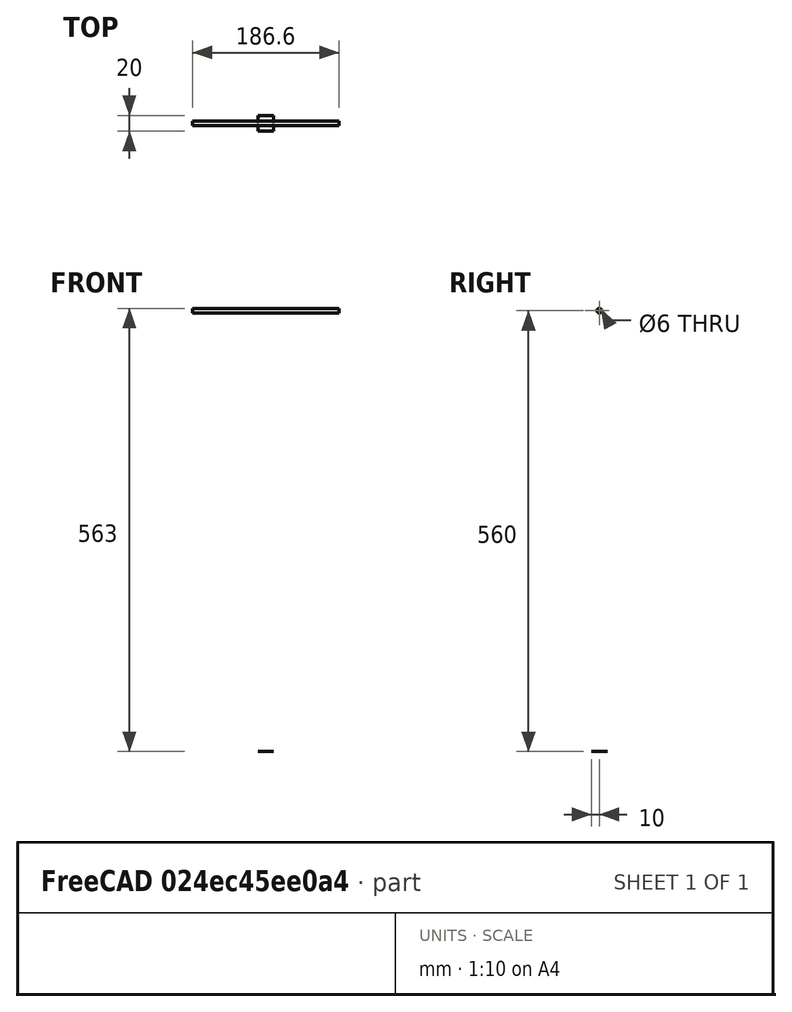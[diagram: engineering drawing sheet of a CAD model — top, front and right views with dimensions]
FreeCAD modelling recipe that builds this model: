
FCSTD DOCUMENT  (FreeCAD 0.19R18044 (Git))
Label: lift-middle-stage
License: Public Domain
LicenseURL: http://en.wikipedia.org/wiki/Public_domain
objects: App::FeaturePython×44, Part::FeaturePython×34, App::Link×6, App::LinkElement×4
note: 33 computed .brp shape members not serialized (recipe doc carries the construction recipe); baked Part::Feature solids carry a one-line shape summary decoded from their .brp
EXTERNAL_REF file=../parts/lift/middle-stage-actuator-rod.FCStd obj=Assembly
EXTERNAL_REF file=../parts/lift/middle-stage-beam.FCStd obj=Assembly001
EXTERNAL_REF file=../parts/lift/middle-stage-beam.FCStd obj=Assembly
EXTERNAL_REF file=../parts/common/linear-actuator-400.FCStd obj=Assembly004
EXTERNAL_REF file=../parts/common/rail-450.FCStd obj=Assembly002
EXTERNAL_REF file=../parts/common/rail-450.FCStd obj=Assembly

FEATURE [App::Link] Link  label="middle-stage-actuator-rod"
  LinkPlacement = pos=(0,-6.67572e-05,560) rot=(0,0,1;0rad)
  LinkedObject = -> <external ../parts/lift/middle-stage-actuator-rod.FCStd>#Assembly
  Placement = pos=(0,-6.67572e-05,560) rot=(0,0,1;0rad)
FEATURE [App::Link] Link001  label="middle-stage-beam-left"
  LinkPlacement = pos=(71.3,-24.5001,10.0001) rot=(0,0,1;0rad)
  LinkedObject = -> <external ../parts/lift/middle-stage-beam.FCStd>#Assembly001
  Placement = pos=(71.3,-24.5001,10.0001) rot=(0,0,1;0rad)
FEATURE [App::Link] Link002  label="middle-stage-beam-right"
  LinkPlacement = pos=(49.7,-24.5001,10.0001) rot=(0,0,1;0rad)
  LinkedObject = -> <external ../parts/lift/middle-stage-beam.FCStd>#Assembly
  Placement = pos=(49.7,-24.5001,10.0001) rot=(0,0,1;0rad)
FEATURE [App::Link] Link003  label="actuator_a"
  LinkPlacement = pos=(7.1213e-12,-6.67572e-05,44.0001) rot=(0,0,1;3.14159rad)
  LinkedObject = -> <external ../parts/common/linear-actuator-400.FCStd>#Assembly004
  Placement = pos=(7.1213e-12,-6.67572e-05,44.0001) rot=(0,0,1;3.14159rad)
FEATURE [App::LinkElement] Link004_i0  label="left"
  LinkPlacement = pos=(106,-6.67572e-05,565) rot=(0.57735,-0.57735,-0.57735;2.0944rad)
  LinkedObject = -> <external ../parts/common/rail-450.FCStd>#Assembly002
  Placement = pos=(106,-6.67572e-05,565) rot=(0.57735,-0.57735,-0.57735;2.0944rad)
FEATURE [App::LinkElement] Link004_i1  label="right"
  LinkPlacement = pos=(-106,-6.67572e-05,565) rot=(0.57735,0.57735,0.57735;2.0944rad)
  LinkedObject = -> <external ../parts/common/rail-450.FCStd>#Assembly002
  Placement = pos=(-106,-6.67572e-05,565) rot=(0.57735,0.57735,0.57735;2.0944rad)
FEATURE [App::Link] Link004  label="rail top"
  ElementCount = 2
  ElementList = -> [Link004_i0,Link004_i1]
  LinkedObject = -> <external ../parts/common/rail-450.FCStd>#Assembly002
FEATURE [App::LinkElement] Link005_i0  label="rail-upper-left"
  LinkPlacement = pos=(93.3,-49.0001,610) rot=(0.57735,0.57735,0.57735;2.0944rad)
  LinkedObject = -> <external ../parts/common/rail-450.FCStd>#Assembly
  Placement = pos=(93.3,-49.0001,610) rot=(0.57735,0.57735,0.57735;2.0944rad)
FEATURE [App::LinkElement] Link005_i1  label="rail-upper-right"
  LinkPlacement = pos=(-93.3,-49.0001,610) rot=(0.57735,-0.57735,-0.57735;2.0944rad)
  LinkedObject = -> <external ../parts/common/rail-450.FCStd>#Assembly
  Placement = pos=(-93.3,-49.0001,610) rot=(0.57735,-0.57735,-0.57735;2.0944rad)
FEATURE [App::Link] Link005  label="rail bottom"
  ElementCount = 2
  ElementList = -> [Link005_i0,Link005_i1]
  LinkedObject = -> <external ../parts/common/rail-450.FCStd>#Assembly
FEATURE [Part::FeaturePython] Parts002  label="Parts"  # WARN: FeaturePython — macro-defined, semantics opaque (R4)
  Group = -> [Origin004,Link,Link001,Link002,Link003,Link004,Link005]
  GroupMode = 0
FEATURE [Part::FeaturePython] Assembly002  label="lift-middle-stage"  # WARN: FeaturePython — macro-defined, semantics opaque (R4)
  AutoRelax = true
  BuildShape = 0
  Freeze = false
  Group = -> [Constraints002,Elements002,Parts002]
  GroupMode = 1
  SolverType = 1
  Verbose = false
  _SolverType = 1
  _Version = 1
FEATURE [App::FeaturePython] Constraints002  # WARN: FeaturePython — macro-defined, semantics opaque (R4)
  Group = -> [Constraint,Constraint003,Constraint004,Constraint005,Constraint006,Constraint007,Constraint008,Constraint009,Constraint010,Constraint011,Constraint012,Constraint013,Constraint014,Constraint015]
  GroupMode = 1
  _Version = 1
FEATURE [App::FeaturePython] Elements002  label="Elements"  # WARN: FeaturePython — macro-defined, semantics opaque (R4)
  Group = -> [_Element,_Element001,_Element002,_Element003,_Element004,_Element005,_Element006,_Element007,_Element008,_Element009,_Element010,_Element011,_Element012,_Element013,_Element014,_Element015,_Element016,_Element017,_Element018,_Element019,_Element020,_Element021,_Element022,_Element023,_Element024,Element,Element001,_Element025,_Element026,Element002,Element003,Element004]
  GroupMode = 1
FEATURE [App::FeaturePython] Constraint  label="Locked"  # WARN: FeaturePython — macro-defined, semantics opaque (R4)
  ConstraintType = 0
  Disabled = false
  Group = -> [ElementLink]
  GroupMode = 1
  _ConstraintType = 0
  _Parent = -> Constraints002
FEATURE [App::FeaturePython] ElementLink  label="_Element"  # link proxy (typed FeaturePython)
  LinkTransform = true
  LinkedObject = -> _Element
  _Parent = -> Constraint
FEATURE [Part::FeaturePython] _Element  # link proxy (typed FeaturePython)
  Detach = false
  LinkTransform = true
  LinkedObject = -> Link [1.$Element003.]
  _Parent = -> Elements002
FEATURE [Part::FeaturePython] _Element001  # link proxy (typed FeaturePython)
  Detach = false
  LinkTransform = true
  LinkedObject = -> Link001 [1.$actuator-rod-hole.]
  _Parent = -> Elements002
FEATURE [Part::FeaturePython] _Element002  # link proxy (typed FeaturePython)
  Detach = false
  LinkTransform = true
  LinkedObject = -> Link [1.$left.]
  _Parent = -> Elements002
FEATURE [Part::FeaturePython] _Element003  # link proxy (typed FeaturePython)
  Detach = false
  LinkTransform = true
  LinkedObject = -> Link002 [1.$actuator_rod_hole.]
  _Parent = -> Elements002
FEATURE [Part::FeaturePython] _Element004  # link proxy (typed FeaturePython)
  Detach = false
  LinkTransform = true
  LinkedObject = -> Link [1.$right.]
  _Parent = -> Elements002
FEATURE [App::FeaturePython] Constraint003  label="PlaneCoincident002"  # WARN: FeaturePython — macro-defined, semantics opaque (R4)
  Angle = 0
  AnglePitch = 0
  AngleRoll = 0
  Cascade = false
  ConstraintType = 2
  Disabled = false
  Group = -> [ElementLink005,ElementLink006]
  GroupMode = 1
  LockAngle = false
  Multiply = false
  OffsetX = 0
  OffsetY = 0
  _ConstraintType = 35
  _Parent = -> Constraints002
FEATURE [App::FeaturePython] ElementLink005  label="_Element005"  # link proxy (typed FeaturePython)
  LinkTransform = true
  LinkedObject = -> _Element005
  _Parent = -> Constraint003
FEATURE [Part::FeaturePython] _Element005  # link proxy (typed FeaturePython)
  Detach = false
  LinkTransform = true
  LinkedObject = -> Link [1.$center.]
  _Parent = -> Elements002
FEATURE [App::FeaturePython] ElementLink006  label="_Element006"  # link proxy (typed FeaturePython)
  LinkTransform = true
  LinkedObject = -> _Element006
  _Parent = -> Constraint003
FEATURE [Part::FeaturePython] _Element006  # link proxy (typed FeaturePython)
  Detach = false
  LinkTransform = true
  LinkedObject = -> Link003 [1.$mount_top.]
  _Parent = -> Elements002
FEATURE [App::FeaturePython] Constraint004  label="PlaneCoincident003"  # WARN: FeaturePython — macro-defined, semantics opaque (R4)
  Angle = 0
  AnglePitch = 0
  AngleRoll = 0
  Cascade = false
  ConstraintType = 2
  Disabled = false
  Group = -> [ElementLink007,ElementLink008]
  GroupMode = 1
  LockAngle = false
  Multiply = false
  Offset = 1
  OffsetX = 0
  OffsetY = 0
  _ConstraintType = 35
  _Parent = -> Constraints002
FEATURE [App::FeaturePython] ElementLink007  label="_Element007"  # link proxy (typed FeaturePython)
  LinkTransform = true
  LinkedObject = -> _Element007
  _Parent = -> Constraint004
FEATURE [Part::FeaturePython] _Element007  # link proxy (typed FeaturePython)
  Detach = false
  LinkTransform = true
  LinkedObject = -> Link005 [Link005_i0.1.$mount_top.]
  _Parent = -> Elements002
FEATURE [App::FeaturePython] ElementLink008  label="_Element008"  # link proxy (typed FeaturePython)
  LinkTransform = true
  LinkedObject = -> _Element008
  _Parent = -> Constraint004
FEATURE [Part::FeaturePython] _Element008  # link proxy (typed FeaturePython)
  Detach = false
  LinkTransform = true
  LinkedObject = -> Link001 [1.$rail_upper_top.]
  _Parent = -> Elements002
FEATURE [App::FeaturePython] Constraint005  label="PlaneCoincident004"  # WARN: FeaturePython — macro-defined, semantics opaque (R4)
  Angle = 0
  AnglePitch = 0
  AngleRoll = 0
  Cascade = false
  ConstraintType = 2
  Disabled = false
  Group = -> [ElementLink009,ElementLink010]
  GroupMode = 1
  LockAngle = false
  Multiply = false
  Offset = 1
  OffsetX = 0
  OffsetY = 0
  _ConstraintType = 35
  _Parent = -> Constraints002
FEATURE [App::FeaturePython] ElementLink009  label="_Element009"  # link proxy (typed FeaturePython)
  LinkTransform = true
  LinkedObject = -> _Element009
  _Parent = -> Constraint005
FEATURE [Part::FeaturePython] _Element009  # link proxy (typed FeaturePython)
  Detach = false
  LinkTransform = true
  LinkedObject = -> Link001 [1.$rail_upper_bottom.]
  _Parent = -> Elements002
FEATURE [App::FeaturePython] ElementLink010  label="_Element010"  # link proxy (typed FeaturePython)
  LinkTransform = true
  LinkedObject = -> _Element010
  _Parent = -> Constraint005
FEATURE [Part::FeaturePython] _Element010  # link proxy (typed FeaturePython)
  Detach = false
  LinkTransform = true
  LinkedObject = -> Link005 [Link005_i0.1.$mount_bottom.]
  _Parent = -> Elements002
FEATURE [App::FeaturePython] Constraint006  label="PlaneCoincident005"  # WARN: FeaturePython — macro-defined, semantics opaque (R4)
  Angle = 0
  AnglePitch = 0
  AngleRoll = 0
  Cascade = false
  ConstraintType = 2
  Disabled = false
  Group = -> [ElementLink011,ElementLink012]
  GroupMode = 1
  LockAngle = false
  Multiply = false
  Offset = -1
  OffsetX = 0
  OffsetY = 0
  _ConstraintType = 35
  _Parent = -> Constraints002
FEATURE [App::FeaturePython] ElementLink011  label="_Element011"  # link proxy (typed FeaturePython)
  LinkTransform = true
  LinkedObject = -> _Element011
  _Parent = -> Constraint006
FEATURE [Part::FeaturePython] _Element011  # link proxy (typed FeaturePython)
  Detach = false
  LinkTransform = true
  LinkedObject = -> Link005 [Link005_i1.1.$mount_top.]
  _Parent = -> Elements002
FEATURE [App::FeaturePython] ElementLink012  label="_Element012"  # link proxy (typed FeaturePython)
  LinkTransform = true
  LinkedObject = -> _Element012
  _Parent = -> Constraint006
FEATURE [Part::FeaturePython] _Element012  # link proxy (typed FeaturePython)
  Detach = false
  LinkTransform = true
  LinkedObject = -> Link002 [1.$rail_upper_top.]
  _Parent = -> Elements002
FEATURE [App::FeaturePython] Constraint007  label="PlaneCoincident006"  # WARN: FeaturePython — macro-defined, semantics opaque (R4)
  Angle = 0
  AnglePitch = 0
  AngleRoll = 0
  Cascade = false
  ConstraintType = 2
  Disabled = false
  Group = -> [ElementLink013,ElementLink014]
  GroupMode = 1
  LockAngle = false
  Multiply = false
  Offset = -1
  OffsetX = 0
  OffsetY = 0
  _ConstraintType = 35
  _Parent = -> Constraints002
FEATURE [App::FeaturePython] ElementLink013  label="_Element013"  # link proxy (typed FeaturePython)
  LinkTransform = true
  LinkedObject = -> _Element013
  _Parent = -> Constraint007
FEATURE [Part::FeaturePython] _Element013  # link proxy (typed FeaturePython)
  Detach = false
  LinkTransform = true
  LinkedObject = -> Link002 [1.$rail_upper_bottom.]
  _Parent = -> Elements002
FEATURE [App::FeaturePython] ElementLink014  label="_Element014"  # link proxy (typed FeaturePython)
  LinkTransform = true
  LinkedObject = -> _Element014
  _Parent = -> Constraint007
FEATURE [Part::FeaturePython] _Element014  # link proxy (typed FeaturePython)
  Detach = false
  LinkTransform = true
  LinkedObject = -> Link005 [Link005_i1.1.$mount_bottom.]
  _Parent = -> Elements002
FEATURE [App::FeaturePython] Constraint008  label="PlaneCoincident007"  # WARN: FeaturePython — macro-defined, semantics opaque (R4)
  Angle = 0
  AnglePitch = 0
  AngleRoll = 0
  Cascade = false
  ConstraintType = 2
  Disabled = false
  Group = -> [ElementLink015,ElementLink016]
  GroupMode = 1
  LockAngle = false
  Multiply = false
  OffsetX = 0
  OffsetY = 0
  _ConstraintType = 35
  _Parent = -> Constraints002
FEATURE [App::FeaturePython] ElementLink015  label="_Element015"  # link proxy (typed FeaturePython)
  LinkTransform = true
  LinkedObject = -> _Element015
  _Parent = -> Constraint008
FEATURE [Part::FeaturePython] _Element015  # link proxy (typed FeaturePython)
  Detach = false
  LinkTransform = true
  LinkedObject = -> Link001 [1.$rail_middle_top.]
  _Parent = -> Elements002
FEATURE [App::FeaturePython] ElementLink016  label="_Element016"  # link proxy (typed FeaturePython)
  LinkTransform = true
  LinkedObject = -> _Element016
  _Parent = -> Constraint008
FEATURE [Part::FeaturePython] _Element016  # link proxy (typed FeaturePython)
  Detach = false
  LinkTransform = true
  LinkedObject = -> Link004 [Link004_i0.1.$mount_top.]
  _Parent = -> Elements002
FEATURE [Part::FeaturePython] _Element017  # link proxy (typed FeaturePython)
  Detach = false
  LinkTransform = true
  LinkedObject = -> Link001 [1.$rail_middle_bottom.]
  _Parent = -> Elements002
FEATURE [Part::FeaturePython] _Element018  # link proxy (typed FeaturePython)
  Detach = false
  LinkTransform = true
  LinkedObject = -> Link004 [Link004_i0.1.$mount_bottom.]
  _Parent = -> Elements002
FEATURE [App::FeaturePython] Constraint009  label="PlaneCoincident008"  # WARN: FeaturePython — macro-defined, semantics opaque (R4)
  Angle = 0
  AnglePitch = 0
  AngleRoll = 0
  Cascade = false
  ConstraintType = 2
  Disabled = false
  Group = -> [ElementLink017,ElementLink018]
  GroupMode = 1
  LockAngle = false
  Multiply = false
  OffsetX = 0
  OffsetY = 0
  _ConstraintType = 35
  _Parent = -> Constraints002
FEATURE [App::FeaturePython] ElementLink017  label="_Element019"  # link proxy (typed FeaturePython)
  LinkTransform = true
  LinkedObject = -> _Element019
  _Parent = -> Constraint009
FEATURE [Part::FeaturePython] _Element019  # link proxy (typed FeaturePython)
  Detach = false
  LinkTransform = true
  LinkedObject = -> Link001 [1.$rail_middle_middle.]
  _Parent = -> Elements002
FEATURE [App::FeaturePython] ElementLink018  label="_Element020"  # link proxy (typed FeaturePython)
  LinkTransform = true
  LinkedObject = -> _Element020
  _Parent = -> Constraint009
FEATURE [Part::FeaturePython] _Element020  # link proxy (typed FeaturePython)
  Detach = false
  LinkTransform = true
  LinkedObject = -> Link004 [Link004_i0.1.$mount_middle.]
  _Parent = -> Elements002
FEATURE [App::FeaturePython] Constraint010  label="PlaneCoincident"  # WARN: FeaturePython — macro-defined, semantics opaque (R4)
  Angle = 0
  AnglePitch = 0
  AngleRoll = 0
  Cascade = false
  ConstraintType = 2
  Disabled = false
  Group = -> [ElementLink019,ElementLink020]
  GroupMode = 1
  LockAngle = false
  Multiply = false
  OffsetX = 0
  OffsetY = 0
  _ConstraintType = 35
  _Parent = -> Constraints002
FEATURE [App::FeaturePython] ElementLink019  label="_Element004"  # link proxy (typed FeaturePython)
  LinkTransform = true
  LinkedObject = -> _Element004
  _Parent = -> Constraint010
FEATURE [App::FeaturePython] ElementLink020  label="_Element001"  # link proxy (typed FeaturePython)
  LinkTransform = true
  LinkedObject = -> _Element001
  _Parent = -> Constraint010
FEATURE [App::FeaturePython] Constraint011  label="PlaneCoincident009"  # WARN: FeaturePython — macro-defined, semantics opaque (R4)
  Angle = 0
  AnglePitch = 0
  AngleRoll = 0
  Cascade = false
  ConstraintType = 2
  Disabled = false
  Group = -> [ElementLink021,ElementLink022]
  GroupMode = 1
  LockAngle = false
  Multiply = false
  OffsetX = 0
  OffsetY = 0
  _ConstraintType = 35
  _Parent = -> Constraints002
FEATURE [App::FeaturePython] ElementLink021  label="_Element002"  # link proxy (typed FeaturePython)
  LinkTransform = true
  LinkedObject = -> _Element002
  _Parent = -> Constraint011
FEATURE [App::FeaturePython] ElementLink022  label="_Element003"  # link proxy (typed FeaturePython)
  LinkTransform = true
  LinkedObject = -> _Element003
  _Parent = -> Constraint011
FEATURE [App::FeaturePython] Constraint012  label="PlaneCoincident010"  # WARN: FeaturePython — macro-defined, semantics opaque (R4)
  Angle = 0
  AnglePitch = 0
  AngleRoll = 0
  Cascade = false
  ConstraintType = 2
  Disabled = false
  Group = -> [ElementLink023,ElementLink024]
  GroupMode = 1
  LockAngle = false
  Multiply = false
  OffsetX = 0
  OffsetY = 0
  _ConstraintType = 35
  _Parent = -> Constraints002
FEATURE [App::FeaturePython] ElementLink023  label="_Element021"  # link proxy (typed FeaturePython)
  LinkTransform = true
  LinkedObject = -> _Element021
  _Parent = -> Constraint012
FEATURE [Part::FeaturePython] _Element021  # link proxy (typed FeaturePython)
  Detach = false
  LinkTransform = true
  LinkedObject = -> Link002 [1.$rail_middle_top.]
  _Parent = -> Elements002
FEATURE [App::FeaturePython] ElementLink024  label="_Element022"  # link proxy (typed FeaturePython)
  LinkTransform = true
  LinkedObject = -> _Element022
  _Parent = -> Constraint012
FEATURE [Part::FeaturePython] _Element022  # link proxy (typed FeaturePython)
  Detach = false
  LinkTransform = true
  LinkedObject = -> Link004 [Link004_i1.1.$mount_top.]
  _Parent = -> Elements002
FEATURE [App::FeaturePython] Constraint013  label="PlaneCoincident011"  # WARN: FeaturePython — macro-defined, semantics opaque (R4)
  Angle = 0
  AnglePitch = 0
  AngleRoll = 0
  Cascade = false
  ConstraintType = 2
  Disabled = false
  Group = -> [ElementLink025,ElementLink026]
  GroupMode = 1
  LockAngle = false
  Multiply = false
  OffsetX = 0
  OffsetY = 0
  _ConstraintType = 35
  _Parent = -> Constraints002
FEATURE [App::FeaturePython] ElementLink025  label="_Element023"  # link proxy (typed FeaturePython)
  LinkTransform = true
  LinkedObject = -> _Element023
  _Parent = -> Constraint013
FEATURE [Part::FeaturePython] _Element023  # link proxy (typed FeaturePython)
  Detach = false
  LinkTransform = true
  LinkedObject = -> Link002 [1.$rail_middle_middle.]
  _Parent = -> Elements002
FEATURE [App::FeaturePython] ElementLink026  label="_Element024"  # link proxy (typed FeaturePython)
  LinkTransform = true
  LinkedObject = -> _Element024
  _Parent = -> Constraint013
FEATURE [Part::FeaturePython] _Element024  # link proxy (typed FeaturePython)
  Detach = false
  LinkTransform = true
  LinkedObject = -> Link004 [Link004_i1.1.$mount_middle.]
  _Parent = -> Elements002
FEATURE [Part::FeaturePython] Element  # link proxy (typed FeaturePython)
  Detach = false
  LinkTransform = true
  LinkedObject = -> Link001 [1.$base_mount_rear.]
  _Parent = -> Elements002
FEATURE [Part::FeaturePython] Element001  # link proxy (typed FeaturePython)
  Detach = false
  LinkTransform = true
  LinkedObject = -> Link002 [1.$base_mount_rear.]
  _Parent = -> Elements002
FEATURE [App::FeaturePython] Constraint014  label="MultiParallel"  # WARN: FeaturePython — macro-defined, semantics opaque (R4)
  Angle = 0
  AnglePitch = 0
  AngleRoll = 0
  ConstraintType = 6
  Disabled = false
  Group = -> [ElementLink027,ElementLink028,ElementLink029]
  GroupMode = 1
  LockAngle = false
  _ConstraintType = 291
  _Parent = -> Constraints002
FEATURE [App::FeaturePython] ElementLink027  label="Element001"  # link proxy (typed FeaturePython)
  LinkTransform = true
  LinkedObject = -> Element001
  _Parent = -> Constraint014
FEATURE [App::FeaturePython] ElementLink028  label="Element"  # link proxy (typed FeaturePython)
  LinkTransform = true
  LinkedObject = -> Element
  _Parent = -> Constraint014
FEATURE [App::FeaturePython] ElementLink029  label="_Element025"  # link proxy (typed FeaturePython)
  LinkTransform = true
  LinkedObject = -> _Element025
  _Parent = -> Constraint014
FEATURE [Part::FeaturePython] _Element025  # link proxy (typed FeaturePython)
  Detach = false
  LinkTransform = true
  LinkedObject = -> Link003 [1.$_Element.]
  _Parent = -> Elements002
FEATURE [App::FeaturePython] Constraint015  label="MultiParallel001"  # WARN: FeaturePython — macro-defined, semantics opaque (R4)
  Angle = 0
  AnglePitch = 0
  AngleRoll = 0
  ConstraintType = 6
  Disabled = false
  Group = -> [ElementLink030,ElementLink031]
  GroupMode = 1
  LockAngle = false
  _ConstraintType = 291
  _Parent = -> Constraints002
FEATURE [App::FeaturePython] ElementLink030  label="_Element026"  # link proxy (typed FeaturePython)
  LinkTransform = true
  LinkedObject = -> _Element026
  _Parent = -> Constraint015
FEATURE [Part::FeaturePython] _Element026  # link proxy (typed FeaturePython)
  Detach = false
  LinkTransform = true
  LinkedObject = -> Origin004 [XY_Plane004.]
  _Parent = -> Elements002
FEATURE [App::FeaturePython] ElementLink031  label="Element"  # link proxy (typed FeaturePython)
  LinkTransform = true
  LinkedObject = -> Element
  _Parent = -> Constraint015
FEATURE [Part::FeaturePython] Element002  # link proxy (typed FeaturePython)
  Detach = false
  LinkTransform = true
  LinkedObject = -> Link005 [Link005_i1.1.$slide_axis.]
  _Parent = -> Elements002
FEATURE [Part::FeaturePython] Element003  # link proxy (typed FeaturePython)
  Detach = false
  LinkTransform = true
  LinkedObject = -> Link005 [Link005_i0.1.$slide_axis.]
  _Parent = -> Elements002
FEATURE [Part::FeaturePython] Element004  # link proxy (typed FeaturePython)
  Detach = false
  LinkTransform = true
  LinkedObject = -> Link004 [Link004_i1.1.$slide_axis.]
  _Parent = -> Elements002

RESOLVED EXTERNAL PARTS (link-assembly join: the EXTERNAL_REF files above that resolve inside this repo's crawl, each included once):
---- part ../parts/common/linear-actuator-400.FCStd = doc fcstd_0eb58a5116f6 ----
FCSTD DOCUMENT  (FreeCAD 0.19R18044 (Git))
Label: linear-actuator-400
License: Public Domain
LicenseURL: http://en.wikipedia.org/wiki/Public_domain
objects: Part::FeaturePython×21, App::FeaturePython×19, Sketcher::SketchObject×15, PartDesign::Pad×8, PartDesign::Pocket×6, PartDesign::Body×4, PartDesign::Hole×1
note: 66 computed .brp shape members not serialized (recipe doc carries the construction recipe); baked Part::Feature solids carry a one-line shape summary decoded from their .brp

FEATURE [Sketcher::SketchObject] Sketch
  MapMode = 5
  Support = -> [XY_Plane]
  sketch-geometry (6):
    g0: LineSegment StartX=-10 StartY=20 StartZ=0 EndX=-20 EndY=11.609 EndZ=0
    g1: LineSegment StartX=-20 StartY=11.609 StartZ=0 EndX=-20 EndY=-35 EndZ=0
    g2: LineSegment StartX=20 StartY=-35 StartZ=0 EndX=20 EndY=11.609 EndZ=0
    g3: LineSegment StartX=20 StartY=11.609 StartZ=0 EndX=10 EndY=20 EndZ=0
    g4: LineSegment StartX=10 StartY=20 StartZ=0 EndX=-10 EndY=20 EndZ=0
    g5: ArcOfCircle CenterX=-4e-16 CenterY=-35 CenterZ=0 NormalX=0 NormalY=0 NormalZ=1 AngleXU=0 Radius=20 StartAngle=3.14159 EndAngle=6.28319
  constraints (18):
    c: Coincident(g0,g1)
    c: Vertical(g1)
    c: Vertical(g2)
    c: Coincident(g2,g3)
    c: Coincident(g3,g4)
    c: Coincident(g4,g0)
    c: Horizontal(g4)
    c: Symmetric(g0,g2,g-2)
    c: Equal(g0,g3)
    c: Coincident(g5,g1)
    c: Coincident(g5,g2)
    c: Radius(g5) = 20
    c: Horizontal(g5,g2)
    c: Horizontal(g2,g1)
    c: DistanceY(g2,g3) = 55
    c: DistanceY(g-1,g3) = 20
    c: Distance(g4) = 20
    c: Angle(g1,g0) = 2.26893
FEATURE [PartDesign::Pad] Pad  label="base"
  ClaimChildren = false
  Length = 22
  Length2 = 100
  Profile = -> Sketch
  Type = 0
FEATURE [Sketcher::SketchObject] Sketch001
  MapMode = 5
  Placement = pos=(0,0,0) rot=(1,0,0;3.14159rad)
  Support = -> [Pad]
  sketch-geometry (9):
    g0: LineSegment StartX=-4.3589 StartY=9 StartZ=0 EndX=4.3589 EndY=9 EndZ=0
    g1: LineSegment StartX=9 StartY=4.3589 StartZ=0 EndX=9 EndY=-4.3589 EndZ=0
    g2: LineSegment StartX=4.3589 StartY=-9 StartZ=0 EndX=-4.3589 EndY=-9 EndZ=0
    g3: LineSegment StartX=-9 StartY=-4.3589 StartZ=0 EndX=-9 EndY=4.3589 EndZ=0
    g4: Circle [constr] CenterX=0 CenterY=0 CenterZ=0 NormalX=0 NormalY=0 NormalZ=1 AngleXU=0 Radius=10
    g5: ArcOfCircle CenterX=0 CenterY=0 CenterZ=0 NormalX=0 NormalY=0 NormalZ=1 AngleXU=0 Radius=10 StartAngle=2.02182 EndAngle=2.69057
    g6: ArcOfCircle CenterX=0 CenterY=0 CenterZ=0 NormalX=0 NormalY=0 NormalZ=1 AngleXU=0 Radius=10 StartAngle=0.451027 EndAngle=1.11977
    g7: ArcOfCircle CenterX=0 CenterY=0 CenterZ=0 NormalX=0 NormalY=0 NormalZ=1 AngleXU=0 Radius=10 StartAngle=5.16342 EndAngle=5.83216
    g8: ArcOfCircle CenterX=0 CenterY=0 CenterZ=0 NormalX=0 NormalY=0 NormalZ=1 AngleXU=0 Radius=10 StartAngle=3.59262 EndAngle=4.26136
  constraints (25):
    c: Horizontal(g0)
    c: Vertical(g1)
    c: Vertical(g3)
    c: Coincident(g4,g-1)
    c: Equal(g0,g1)
    c: Radius(g4) = 10
    c: Coincident(g5,g3)
    c: Coincident(g0,g5)
    c: Coincident(g-1,g5)
    c: Radius(g5) = 10
    c: Coincident(g2,g8)
    c: Coincident(g2,g7)
    c: Coincident(g1,g7)
    c: Coincident(g1,g6)
    c: Coincident(g0,g6)
    c: Coincident(g8,g5)
    c: Coincident(g8,g3)
    c: Coincident(g7,g5)
    c: Coincident(g6,g5)
    c: Radius(g6) = 10
    c: Radius(g7) = 10
    c: DistanceY(g2,g0) = 18
    c: DistanceX(g3,g1) = 18
    c: Symmetric(g2,g2,g-2)
    c: Vertical(g0,g2)
FEATURE [PartDesign::Pad] Pad001  label="foot"
  BaseFeature = -> Pad
  ClaimChildren = false
  Length = 19
  Length2 = 100
  Profile = -> Sketch001
  Type = 0
FEATURE [Sketcher::SketchObject] Sketch002
  MapMode = 5
  Placement = pos=(-9,0,0) rot=(0.57735,-0.57735,-0.57735;2.0944rad)
  Support = -> [Pad001]
  sketch-geometry (1):
    g0: Circle CenterX=0 CenterY=-11 CenterZ=0 NormalX=0 NormalY=0 NormalZ=1 AngleXU=0 Radius=3.25
  constraints (3):
    c: PointOnObject(g0,g-2)
    c: Diameter(g0) = 6.5
    c: DistanceY(g0,g-1) = 11
FEATURE [PartDesign::Hole] Hole
  BaseFeature = -> Pad001
  ClaimChildren = false
  Depth = 25
  DepthType = 1
  Diameter = 6
  DrillPoint = 1
  DrillPointAngle = 118
  HoleCutCountersinkAngle = 90
  HoleCutDepth = 0
  HoleCutDiameter = 0
  HoleCutType = 0
  ModelActualThread = false
  Profile = -> Sketch002
  Tapered = false
  TaperedAngle = 90
  ThreadAngle = 0
  ThreadClass = 0
  ThreadCutOffInner = 0
  ThreadCutOffOuter = 0
  ThreadDirection = 0
  ThreadFit = 0
  ThreadPitch = 0
  ThreadSize = 0
  ThreadType = 0
  Threaded = false
FEATURE [Sketcher::SketchObject] Sketch003
  ExternalGeometry = -> [Hole]
  MapMode = 5
  Placement = pos=(0,0,22) rot=(0,0,1;0rad)
  Support = -> [Hole]
  sketch-geometry (4):
    g0: LineSegment StartX=-15 StartY=1.8e-15 StartZ=0 EndX=-10 EndY=20 EndZ=0
    g1: LineSegment StartX=-10 StartY=20 StartZ=0 EndX=10 EndY=20 EndZ=0
    g2: LineSegment StartX=10 StartY=20 StartZ=0 EndX=15 EndY=-3.6e-15 EndZ=0
    g3: ArcOfCircle CenterX=0 CenterY=0 CenterZ=0 NormalX=0 NormalY=0 NormalZ=1 AngleXU=0 Radius=15 StartAngle=3.14159 EndAngle=6.28319
  constraints (12):
    c: Coincident(g0,g1)
    c: Horizontal(g1)
    c: Coincident(g1,g2)
    c: Coincident(g3,g-1)
    c: Coincident(g3,g0)
    c: Coincident(g3,g2)
    c: Diameter(g3) = 30
    c: PointOnObject(g0,g-3)
    c: DistanceX(g1,g1) = 20
    c: Equal(g2,g0)
    c: Symmetric(g2,g0,g-2)
    c: PointOnObject(g2,g-1)
FEATURE [PartDesign::Pad] Pad002
  BaseFeature = -> Hole
  ClaimChildren = false
  Length = 500
  Length2 = 100
  Profile = -> Sketch003
  Type = 0
FEATURE [Sketcher::SketchObject] Sketch004
  MapMode = 5
  Placement = pos=(0,0,522) rot=(0,0,1;0rad)
  Support = -> [Pad002]
  sketch-geometry (1):
    g0: Circle CenterX=0 CenterY=0 CenterZ=0 NormalX=0 NormalY=0 NormalZ=1 AngleXU=0 Radius=10
  constraints (2):
    c: Coincident(g0,g-1)
    c: Diameter(g0) = 20
FEATURE [PartDesign::Pocket] Pocket
  BaseFeature = -> Pad002
  ClaimChildren = false
  Length = 500
  Length2 = 100
  Profile = -> Sketch004
  Type = 0
FEATURE [Sketcher::SketchObject] Sketch005
  MapMode = 5
  Support = -> [XY_Plane001]
  sketch-geometry (1):
    g0: Circle CenterX=0 CenterY=0 CenterZ=0 NormalX=0 NormalY=0 NormalZ=1 AngleXU=0 Radius=10
  constraints (2):
    c: Coincident(g0,g-1)
    c: Diameter(g0) = 20
FEATURE [PartDesign::Pad] Pad003
  ClaimChildren = false
  Length = 523
  Length2 = 100
  Profile = -> Sketch005
  Type = 0
FEATURE [Sketcher::SketchObject] Sketch006
  ExternalGeometry = -> [Pad003]
  MapMode = 5
  Placement = pos=(0,0,0) rot=(0.57735,0.57735,0.57735;2.0944rad)
  Support = -> [YZ_Plane001]
  sketch-geometry (1):
    g0: Circle CenterX=-1.11e-13 CenterY=514 CenterZ=0 NormalX=0 NormalY=0 NormalZ=1 AngleXU=0 Radius=3.25
  constraints (3):
    c: DistanceY(g0,g-3) = 9
    c: PointOnObject(g0,g-3)
    c: Diameter(g0) = 6.5
FEATURE [PartDesign::Pocket] Pocket001
  BaseFeature = -> Pad003
  ClaimChildren = false
  Length = 5
  Length2 = 100
  Midplane = true
  Profile = -> Sketch006
  Type = 1
FEATURE [PartDesign::Body] Body001  label="piston"
  Group = -> [Sketch005,Pad003,Sketch006,Pocket001]
  Origin = -> Origin001
  Placement = pos=(0,0,22) rot=(0,0,1;0rad)
  SingleSolid = true
  Tip = -> Pocket001
FEATURE [Sketcher::SketchObject] Sketch007
  MapMode = 5
  Placement = pos=(0,0,22) rot=(0,0,1;0rad)
  Support = -> [Pocket]
  sketch-geometry (1):
    g0: Circle CenterX=0 CenterY=-35 CenterZ=0 NormalX=0 NormalY=0 NormalZ=1 AngleXU=0 Radius=19
  constraints (3):
    c: PointOnObject(g0,g-2)
    c: Diameter(g0) = 38
    c: DistanceY(g0,g-1) = 35
FEATURE [PartDesign::Pad] Pad004
  BaseFeature = -> Pocket
  ClaimChildren = false
  Length = 77
  Length2 = 100
  Profile = -> Sketch007
  Type = 0
FEATURE [Sketcher::SketchObject] Sketch008
  MapMode = 5
  Placement = pos=(0,0,99) rot=(0,0,1;0rad)
  Support = -> [Pad004]
  sketch-geometry (1):
    g0: Circle CenterX=0 CenterY=-35 CenterZ=0 NormalX=0 NormalY=0 NormalZ=1 AngleXU=0 Radius=6.25
  constraints (3):
    c: PointOnObject(g0,g-2)
    c: DistanceY(g0,g-1) = 35
    c: Diameter(g0) = 12.5
FEATURE [PartDesign::Pad] Pad005
  BaseFeature = -> Pad004
  ClaimChildren = false
  Length = 2
  Length2 = 100
  Profile = -> Sketch008
  Type = 0
FEATURE [PartDesign::Body] Body  label="actuator base"
  Group = -> [Sketch,Pad,Sketch001,Pad001,Sketch002,Hole,Sketch003,Pad002,Sketch004,Pocket,Sketch007,Pad004,Sketch008,Pad005]
  Origin = -> Origin
  SingleSolid = true
  Tip = -> Pad005
FEATURE [Sketcher::SketchObject] Sketch009
  MapMode = 5
  Placement = pos=(0,0,0) rot=(1,0,0;1.5708rad)
  Support = -> [XZ_Plane002]
  sketch-geometry (7):
    g0: LineSegment StartX=-8.5 StartY=1e-15 StartZ=0 EndX=-8.5 EndY=-36.5 EndZ=0
    g1: LineSegment StartX=-8.5 StartY=-36.5 StartZ=0 EndX=49.5 EndY=-36.5 EndZ=0
    g2: LineSegment StartX=49.5 StartY=-36.5 StartZ=0 EndX=49.5 EndY=-21.5 EndZ=0
    g3: LineSegment StartX=49.5 StartY=-21.5 StartZ=0 EndX=3.04099 EndY=7.9374 EndZ=0
    g4: ArcOfCircle CenterX=0 CenterY=0 CenterZ=0 NormalX=0 NormalY=0 NormalZ=1 AngleXU=0 Radius=8.5 StartAngle=1.20492 EndAngle=3.14159
    g5: Circle CenterX=0 CenterY=0 CenterZ=0 NormalX=0 NormalY=0 NormalZ=1 AngleXU=0 Radius=3
    g6: GeomPoint X=1.97567e-07 Y=8.5 Z=0
  constraints (19):
    c: Vertical(g0)
    c: Coincident(g0,g1)
    c: Horizontal(g1)
    c: Coincident(g1,g2)
    c: Vertical(g2)
    c: Coincident(g2,g3)
    c: Coincident(g4,g-1)
    c: Coincident(g4,g0)
    c: Coincident(g4,g3)
    c: Coincident(g5,g4)
    c: Distance(g1) = 58
    c: Distance(g0) = 36.5
    c: Distance(g2) = 15
    c: Diameter(g5) = 6
    c: DistanceX(g0,g4) = 8.5
    c: PointOnObject(g0,g-1)
    c: PointOnObject(g6,g4)
    c: DistanceY(g0,g6) = 45
    c: Distance(g3) = 55
FEATURE [PartDesign::Pad] Pad006
  ClaimChildren = false
  Length = 25.5
  Length2 = 100
  Midplane = true
  Placement = pos=(0,0,0) rot=(1,0,0;1.5708rad)
  Profile = -> Sketch009
  Type = 0
FEATURE [Sketcher::SketchObject] Sketch010
  ExternalGeometry = -> [Pad006]
  MapMode = 5
  Placement = pos=(-8.5,0,0) rot=(0.707107,0,-0.707107;3.14159rad)
  Support = -> [Pad006]
  sketch-geometry (4):
    g0: LineSegment StartX=-11.5 StartY=9.75 StartZ=0 EndX=33.5 EndY=9.75 EndZ=0
    g1: LineSegment StartX=33.5 StartY=9.75 StartZ=0 EndX=33.5 EndY=-9.75 EndZ=0
    g2: LineSegment StartX=33.5 StartY=-9.75 StartZ=0 EndX=-11.5 EndY=-9.75 EndZ=0
    g3: LineSegment StartX=-11.5 StartY=-9.75 StartZ=0 EndX=-11.5 EndY=9.75 EndZ=0
  constraints (11):
    c: Coincident(g0,g1)
    c: Coincident(g1,g2)
    c: Coincident(g2,g3)
    c: Coincident(g3,g0)
    c: Horizontal(g0)
    c: Horizontal(g2)
    c: Vertical(g3)
    c: Symmetric(g0,g1,g-1)
    c: DistanceX(g0,g-3) = 3
    c: DistanceY(g0,g-3) = 3
    c: Distance(g0) = 45
FEATURE [PartDesign::Pocket] Pocket002
  BaseFeature = -> Pad006
  ClaimChildren = false
  Length = 5
  Length2 = 100
  Placement = pos=(0,0,0) rot=(1,0,0;1.5708rad)
  Profile = -> Sketch010
  Type = 1
FEATURE [Sketcher::SketchObject] Sketch011
  ExternalGeometry = -> [Pocket002]
  MapMode = 5
  Placement = pos=(7.4e-15,0,-33.5) rot=(0,0,1;3.14159rad)
  Support = -> [Pocket002]
  sketch-geometry (5):
    g0: Circle CenterX=-37 CenterY=0 CenterZ=0 NormalX=0 NormalY=0 NormalZ=1 AngleXU=0 Radius=4
    g1: LineSegment StartX=-1.5 StartY=4.25 StartZ=0 EndX=8.5 EndY=4.25 EndZ=0
    g2: LineSegment StartX=-1.5 StartY=-4.25 StartZ=0 EndX=8.5 EndY=-4.25 EndZ=0
    g3: ArcOfCircle CenterX=-1.5 CenterY=4e-16 CenterZ=0 NormalX=0 NormalY=0 NormalZ=1 AngleXU=0 Radius=4.25 StartAngle=1.5708 EndAngle=4.71239
    g4: LineSegment StartX=8.5 StartY=4.25 StartZ=0 EndX=8.5 EndY=-4.25 EndZ=0
  constraints (15):
    c: PointOnObject(g0,g-1)
    c: PointOnObject(g1,g-3)
    c: Horizontal(g1)
    c: PointOnObject(g2,g-3)
    c: Horizontal(g2)
    c: Symmetric(g1,g2,g-1)
    c: Coincident(g3,g2)
    c: Coincident(g3,g1)
    c: DistanceX(g3,g-3) = 10
    c: Distance(g1) = 10
    c: Diameter(g3) = 8.5
    c: Diameter(g0) = 8
    c: DistanceX(g0,g-3) = 45.5
    c: Coincident(g4,g1)
    c: Coincident(g4,g2)
FEATURE [PartDesign::Pocket] Pocket003
  BaseFeature = -> Pocket002
  ClaimChildren = false
  Length = 5
  Length2 = 100
  Placement = pos=(0,0,0) rot=(1,0,0;1.5708rad)
  Profile = -> Sketch011
  Type = 1
FEATURE [PartDesign::Body] Body002  label="bracket bottom"
  Group = -> [Sketch009,Pad006,Sketch010,Pocket002,Sketch011,Pocket003]
  Origin = -> Origin002
  Placement = pos=(0,0,-11) rot=(0,0,1;4.71239rad)
  SingleSolid = true
  Tip = -> Pocket003
FEATURE [Sketcher::SketchObject] Sketch012
  MapMode = 5
  Placement = pos=(0,0,0) rot=(1,0,0;1.5708rad)
  Support = -> [XZ_Plane003]
  sketch-geometry (7):
    g0: LineSegment StartX=-8.5 StartY=1e-15 StartZ=0 EndX=-8.5 EndY=-36.5 EndZ=0
    g1: LineSegment StartX=-8.5 StartY=-36.5 StartZ=0 EndX=49.5 EndY=-36.5 EndZ=0
    g2: LineSegment StartX=49.5 StartY=-36.5 StartZ=0 EndX=49.5 EndY=-21.5 EndZ=0
    g3: LineSegment StartX=49.5 StartY=-21.5 StartZ=0 EndX=3.04099 EndY=7.9374 EndZ=0
    g4: ArcOfCircle CenterX=0 CenterY=0 CenterZ=0 NormalX=0 NormalY=0 NormalZ=1 AngleXU=0 Radius=8.5 StartAngle=1.20492 EndAngle=3.14159
    g5: Circle CenterX=0 CenterY=0 CenterZ=0 NormalX=0 NormalY=0 NormalZ=1 AngleXU=0 Radius=3
    g6: GeomPoint X=2.60784e-05 Y=8.5 Z=0
  constraints (19):
    c: Vertical(g0)
    c: Coincident(g0,g1)
    c: Horizontal(g1)
    c: Coincident(g1,g2)
    c: Vertical(g2)
    c: Coincident(g2,g3)
    c: Coincident(g4,g-1)
    c: Coincident(g4,g0)
    c: Coincident(g4,g3)
    c: Coincident(g5,g4)
    c: Distance(g1) = 58
    c: Distance(g0) = 36.5
    c: Distance(g2) = 15
    c: Diameter(g5) = 6
    c: DistanceX(g0,g4) = 8.5
    c: PointOnObject(g0,g-1)
    c: PointOnObject(g6,g4)
    c: DistanceY(g0,g6) = 45
    c: Distance(g3) = 55
FEATURE [PartDesign::Pad] Pad007
  ClaimChildren = false
  Length = 25.5
  Length2 = 100
  Midplane = true
  Placement = pos=(0,0,0) rot=(1,0,0;1.5708rad)
  Profile = -> Sketch012
  Type = 0
FEATURE [Sketcher::SketchObject] Sketch013
  ExternalGeometry = -> [Pad007]
  MapMode = 5
  Placement = pos=(-8.5,0,0) rot=(0.707107,0,-0.707107;3.14159rad)
  Support = -> [Pad007]
  sketch-geometry (4):
    g0: LineSegment StartX=-11.5 StartY=9.75 StartZ=0 EndX=33.5 EndY=9.75 EndZ=0
    g1: LineSegment StartX=33.5 StartY=9.75 StartZ=0 EndX=33.5 EndY=-9.75 EndZ=0
    g2: LineSegment StartX=33.5 StartY=-9.75 StartZ=0 EndX=-11.5 EndY=-9.75 EndZ=0
    g3: LineSegment StartX=-11.5 StartY=-9.75 StartZ=0 EndX=-11.5 EndY=9.75 EndZ=0
  constraints (11):
    c: Coincident(g0,g1)
    c: Coincident(g1,g2)
    c: Coincident(g2,g3)
    c: Coincident(g3,g0)
    c: Horizontal(g0)
    c: Horizontal(g2)
    c: Vertical(g3)
    c: Symmetric(g0,g1,g-1)
    c: DistanceX(g0,g-3) = 3
    c: DistanceY(g0,g-3) = 3
    c: Distance(g0) = 45
FEATURE [PartDesign::Pocket] Pocket004
  BaseFeature = -> Pad007
  ClaimChildren = false
  Length = 5
  Length2 = 100
  Placement = pos=(0,0,0) rot=(1,0,0;1.5708rad)
  Profile = -> Sketch013
  Type = 1
FEATURE [Sketcher::SketchObject] Sketch014
  ExternalGeometry = -> [Pocket004]
  MapMode = 5
  Placement = pos=(7.4e-15,0,-33.5) rot=(0,0,1;3.14159rad)
  Support = -> [Pocket004]
  sketch-geometry (5):
    g0: Circle CenterX=-37 CenterY=0 CenterZ=0 NormalX=0 NormalY=0 NormalZ=1 AngleXU=0 Radius=4
    g1: LineSegment StartX=-1.5 StartY=4.25 StartZ=0 EndX=8.5 EndY=4.25 EndZ=0
    g2: LineSegment StartX=-1.5 StartY=-4.25 StartZ=0 EndX=8.5 EndY=-4.25 EndZ=0
    g3: ArcOfCircle CenterX=-1.5 CenterY=4e-16 CenterZ=0 NormalX=0 NormalY=0 NormalZ=1 AngleXU=0 Radius=4.25 StartAngle=1.5708 EndAngle=4.71239
    g4: LineSegment StartX=8.5 StartY=4.25 StartZ=0 EndX=8.5 EndY=-4.25 EndZ=0
  constraints (15):
    c: PointOnObject(g0,g-1)
    c: PointOnObject(g1,g-3)
    c: Horizontal(g1)
    c: PointOnObject(g2,g-3)
    c: Horizontal(g2)
    c: Symmetric(g1,g2,g-1)
    c: Coincident(g3,g2)
    c: Coincident(g3,g1)
    c: DistanceX(g3,g-3) = 10
    c: Distance(g1) = 10
    c: Diameter(g3) = 8.5
    c: Diameter(g0) = 8
    c: DistanceX(g0,g-3) = 45.5
    c: Coincident(g4,g1)
    c: Coincident(g4,g2)
FEATURE [PartDesign::Pocket] Pocket005
  BaseFeature = -> Pocket004
  ClaimChildren = false
  Length = 5
  Length2 = 100
  Placement = pos=(0,0,0) rot=(1,0,0;1.5708rad)
  Profile = -> Sketch014
  Type = 1
FEATURE [PartDesign::Body] Body003  label="bracket top"
  Group = -> [Sketch012,Pad007,Sketch013,Pocket004,Sketch014,Pocket005]
  Origin = -> Origin003
  Placement = pos=(2e-15,0,536) rot=(-0.707107,0.707107,0;3.14159rad)
  SingleSolid = true
  Tip = -> Pocket005
FEATURE [App::FeaturePython] Constraints  # WARN: FeaturePython — macro-defined, semantics opaque (R4)
  GroupMode = 1
  _Version = 1
FEATURE [Part::FeaturePython] Parts  label="Parts_Bracket"  # WARN: FeaturePython — macro-defined, semantics opaque (R4)
  Group = -> [Body002]
  GroupMode = 0
FEATURE [App::FeaturePython] Constraints002  # WARN: FeaturePython — macro-defined, semantics opaque (R4)
  GroupMode = 1
  _Version = 1
FEATURE [Part::FeaturePython] Parts002  label="Parts_Piston"  # WARN: FeaturePython — macro-defined, semantics opaque (R4)
  Group = -> [Body001]
  GroupMode = 0
FEATURE [App::FeaturePython] Constraints003  # WARN: FeaturePython — macro-defined, semantics opaque (R4)
  GroupMode = 1
  _Version = 1
FEATURE [Part::FeaturePython] Parts003  label="Parts_Base"  # WARN: FeaturePython — macro-defined, semantics opaque (R4)
  Group = -> [Body]
  GroupMode = 0
FEATURE [Part::FeaturePython] Assembly  label="bracket_a"  # WARN: FeaturePython — macro-defined, semantics opaque (R4)
  AutoRelax = true
  BuildShape = 0
  Freeze = false
  Group = -> [Constraints,Elements,Parts]
  GroupMode = 1
  Placement = pos=(0,2.38419e-06,-20) rot=(0,0,1;0rad)
  SolverType = 1
  Verbose = false
  _SolverType = 1
  _Version = 1
FEATURE [App::FeaturePython] Elements  label="Elements_Bracket"  # WARN: FeaturePython — macro-defined, semantics opaque (R4)
  Group = -> [Element,Element001,Element003]
  GroupMode = 1
FEATURE [Part::FeaturePython] Assembly002  label="piston_a"  # WARN: FeaturePython — macro-defined, semantics opaque (R4)
  AutoRelax = true
  BuildShape = 0
  Freeze = false
  Group = -> [Constraints002,Elements002,Parts002]
  GroupMode = 1
  Placement = pos=(1.7e-15,2.38418e-06,-20) rot=(0,0,1;0rad)
  SolverType = 1
  Verbose = false
  _SolverType = 1
  _Version = 1
FEATURE [App::FeaturePython] Elements002  label="Elements_Piston"  # WARN: FeaturePython — macro-defined, semantics opaque (R4)
  Group = -> [Element006,Element007]
  GroupMode = 1
FEATURE [Part::FeaturePython] Assembly003  label="actuator_base_a"  # WARN: FeaturePython — macro-defined, semantics opaque (R4)
  AutoRelax = true
  BuildShape = 0
  Freeze = false
  Group = -> [Constraints003,Elements003,Parts003]
  GroupMode = 1
  Placement = pos=(4e-16,2.38418e-06,-20) rot=(0,0,1;0rad)
  SolverType = 1
  Verbose = false
  _SolverType = 1
  _Version = 1
FEATURE [App::FeaturePython] Elements003  label="Elements_Base"  # WARN: FeaturePython — macro-defined, semantics opaque (R4)
  Group = -> [Element004,Element005]
  GroupMode = 1
FEATURE [Part::FeaturePython] Assembly004  label="actuator_a"  # WARN: FeaturePython — macro-defined, semantics opaque (R4)
  AutoRelax = true
  BuildShape = 0
  Freeze = false
  Group = -> [Constraints004,Elements004,Parts004]
  GroupMode = 1
  SolverType = 1
  Verbose = false
  _SolverType = 1
  _Version = 1
FEATURE [App::FeaturePython] Constraints004  label="Constraints_Actuator"  # WARN: FeaturePython — macro-defined, semantics opaque (R4)
  Group = -> [Constraint,Constraint001,Constraint002,Constraint003]
  GroupMode = 1
  _Version = 1
FEATURE [App::FeaturePython] Elements004  label="Elements_Actuator"  # WARN: FeaturePython — macro-defined, semantics opaque (R4)
  Group = -> [_Element,_Element001,_Element002,_Element003,_Element004,Element008]
  GroupMode = 1
FEATURE [Part::FeaturePython] Parts004  label="Parts_Actuator"  # WARN: FeaturePython — macro-defined, semantics opaque (R4)
  Group = -> [Assembly003,Assembly002,Assembly]
  GroupMode = 0
FEATURE [Part::FeaturePython] Element  label="actuator_socket_hole"  # link proxy (typed FeaturePython)
  Detach = false
  LinkTransform = true
  LinkedObject = -> Body002 [Pad006.Sketch009.Edge6]
  _Parent = -> Elements
FEATURE [Part::FeaturePython] Element001  label="mount_hole"  # link proxy (typed FeaturePython)
  Detach = false
  LinkTransform = true
  LinkedObject = -> Body002 [Pocket003.Sketch011.Edge1]
  _Parent = -> Elements
FEATURE [Part::FeaturePython] Element003  label="mount_slot"  # link proxy (typed FeaturePython)
  Detach = false
  LinkTransform = true
  LinkedObject = -> Body002 [Pocket003.Sketch011.Edge2]
  _Parent = -> Elements
FEATURE [Part::FeaturePython] Element004  label="mount_bottom"  # link proxy (typed FeaturePython)
  Detach = false
  LinkTransform = true
  LinkedObject = -> Body [Hole.Sketch002.Edge1]
  Offset = pos=(0,0,-9) rot=(0,0,1;0rad)
  Placement = pos=(9,0,0) rot=(0,0,1;0rad)
  _Parent = -> Elements003
FEATURE [Part::FeaturePython] Element005  label="piston_hole"  # link proxy (typed FeaturePython)
  Detach = false
  LinkTransform = true
  LinkedObject = -> Body [Pocket.Sketch004.Edge1]
  _Parent = -> Elements003
FEATURE [Part::FeaturePython] Element006  label="piston_cylinder"  # link proxy (typed FeaturePython)
  Detach = false
  LinkTransform = true
  LinkedObject = -> Body001 [Pad003.Sketch005.Edge1]
  _Parent = -> Elements002
FEATURE [Part::FeaturePython] Element007  label="mount_top"  # link proxy (typed FeaturePython)
  Detach = false
  LinkTransform = true
  LinkedObject = -> Body001 [Pocket001.Sketch006.Edge1]
  _Parent = -> Elements002
FEATURE [App::FeaturePython] Constraint  label="Locked"  # WARN: FeaturePython — macro-defined, semantics opaque (R4)
  ConstraintType = 0
  Disabled = false
  Group = -> [ElementLink]
  GroupMode = 1
  _ConstraintType = 0
  _Parent = -> Constraints004
FEATURE [App::FeaturePython] ElementLink  label="_Element"  # link proxy (typed FeaturePython)
  LinkTransform = true
  LinkedObject = -> _Element
  _Parent = -> Constraint
FEATURE [Part::FeaturePython] _Element  # link proxy (typed FeaturePython)
  Detach = false
  LinkTransform = true
  LinkedObject = -> Assembly [1.$mount_hole.]
  _Parent = -> Elements004
FEATURE [App::FeaturePython] Constraint001  label="PlaneCoincident"  # WARN: FeaturePython — macro-defined, semantics opaque (R4)
  Angle = 0
  AnglePitch = 0
  AngleRoll = 0
  Cascade = false
  ConstraintType = 2
  Disabled = false
  Group = -> [ElementLink001,ElementLink002]
  GroupMode = 1
  LockAngle = false
  Multiply = false
  OffsetX = 0
  OffsetY = 0
  _ConstraintType = 35
  _Parent = -> Constraints004
FEATURE [App::FeaturePython] ElementLink001  label="_Element001"  # link proxy (typed FeaturePython)
  LinkTransform = true
  LinkedObject = -> _Element001
  _Parent = -> Constraint001
FEATURE [Part::FeaturePython] _Element001  # link proxy (typed FeaturePython)
  Detach = false
  LinkTransform = true
  LinkedObject = -> Assembly003 [1.$mount_bottom.]
  _Parent = -> Elements004
FEATURE [App::FeaturePython] ElementLink002  label="_Element002"  # link proxy (typed FeaturePython)
  LinkTransform = true
  LinkedObject = -> _Element002
  _Parent = -> Constraint001
FEATURE [Part::FeaturePython] _Element002  # link proxy (typed FeaturePython)
  Detach = false
  LinkTransform = true
  LinkedObject = -> Assembly [1.$actuator_socket_hole.]
  _Parent = -> Elements004
FEATURE [App::FeaturePython] Constraint002  label="PlaneCoincident001"  # WARN: FeaturePython — macro-defined, semantics opaque (R4)
  Angle = 0
  AnglePitch = 0
  AngleRoll = 0
  Cascade = false
  ConstraintType = 2
  Disabled = false
  Group = -> [ElementLink003,ElementLink004]
  GroupMode = 1
  LockAngle = true
  Multiply = false
  Offset = -500
  OffsetX = 0
  OffsetY = 0
  _ConstraintType = 35
  _Parent = -> Constraints004
FEATURE [App::FeaturePython] ElementLink003  label="_Element003"  # link proxy (typed FeaturePython)
  LinkTransform = true
  LinkedObject = -> _Element003
  _Parent = -> Constraint002
FEATURE [Part::FeaturePython] _Element003  # link proxy (typed FeaturePython)
  Detach = false
  LinkTransform = true
  LinkedObject = -> Assembly002 [1.$piston_cylinder.]
  _Parent = -> Elements004
FEATURE [App::FeaturePython] ElementLink004  label="_Element004"  # link proxy (typed FeaturePython)
  LinkTransform = true
  LinkedObject = -> _Element004
  _Parent = -> Constraint002
FEATURE [Part::FeaturePython] _Element004  # link proxy (typed FeaturePython)
  Detach = false
  LinkTransform = true
  LinkedObject = -> Assembly003 [1.$piston_hole.]
  _Parent = -> Elements004
FEATURE [Part::FeaturePython] Element008  label="mount_top"  # link proxy (typed FeaturePython)
  Detach = false
  LinkTransform = true
  LinkedObject = -> Assembly002 [1.$mount_top.]
  _Parent = -> Elements004
FEATURE [App::FeaturePython] Constraint003  label="MultiParallel"  # WARN: FeaturePython — macro-defined, semantics opaque (R4)
  Angle = 0
  AnglePitch = 0
  AngleRoll = 0
  ConstraintType = 6
  Disabled = false
  Group = -> [ElementLink005,ElementLink006]
  GroupMode = 1
  LockAngle = false
  _ConstraintType = 291
  _Parent = -> Constraints004
FEATURE [App::FeaturePython] ElementLink005  label="_Element003"  # link proxy (typed FeaturePython)
  LinkTransform = true
  LinkedObject = -> _Element003
  _Parent = -> Constraint003
FEATURE [App::FeaturePython] ElementLink006  label="_Element"  # link proxy (typed FeaturePython)
  LinkTransform = true
  LinkedObject = -> _Element
  _Parent = -> Constraint003
---- part ../parts/common/rail-450.FCStd = doc fcstd_040eeb14510a ----
FCSTD DOCUMENT  (FreeCAD 0.19R18044 (Git))
Label: rail-450
License: Public Domain
LicenseURL: http://en.wikipedia.org/wiki/Public_domain
objects: Part::FeaturePython×13, Sketcher::SketchObject×9, PartDesign::Pocket×6, App::FeaturePython×6, PartDesign::Pad×3, PartDesign::Body×3, PartDesign::LinearPattern×3, PartDesign::Line×2
note: 45 computed .brp shape members not serialized (recipe doc carries the construction recipe); baked Part::Feature solids carry a one-line shape summary decoded from their .brp

FEATURE [Sketcher::SketchObject] Sketch
  MapMode = 5
  Placement = pos=(0,0,0) rot=(1,0,0;1.5708rad)
  Support = -> [XZ_Plane]
  sketch-geometry (4):
    g0: LineSegment StartX=-22.5 StartY=12.7 StartZ=0 EndX=22.5 EndY=12.7 EndZ=0
    g1: LineSegment StartX=22.5 StartY=12.7 StartZ=0 EndX=22.5 EndY=0 EndZ=0
    g2: LineSegment StartX=22.5 StartY=0 StartZ=0 EndX=-22.5 EndY=0 EndZ=0
    g3: LineSegment StartX=-22.5 StartY=0 StartZ=0 EndX=-22.5 EndY=12.7 EndZ=0
  constraints (11):
    c: Coincident(g0,g1)
    c: Coincident(g1,g2)
    c: Coincident(g2,g3)
    c: Coincident(g3,g0)
    c: Horizontal(g2)
    c: Vertical(g1)
    c: Vertical(g3)
    c: PointOnObject(g1,g-1)
    c: Symmetric(g0,g0,g-2)
    c: Distance(g0) = 45
    c: Distance(g3) = 12.7
FEATURE [PartDesign::Pad] Pad
  ClaimChildren = false
  Length = 450
  Length2 = 100
  Placement = pos=(0,0,0) rot=(1,0,0;1.5708rad)
  Profile = -> Sketch
  Type = 0
FEATURE [Sketcher::SketchObject] Sketch001
  ExternalGeometry = -> [Pad]
  MapMode = 5
  Placement = pos=(0,-450,-9.9e-14) rot=(1,0,0;1.5708rad)
  Support = -> [Pad]
  sketch-geometry (8):
    g0: LineSegment StartX=-18.5 StartY=12.7 StartZ=0 EndX=-18.5 EndY=11.7 EndZ=0
    g1: LineSegment StartX=-18.5 StartY=11.7 StartZ=0 EndX=-21.5 EndY=11.7 EndZ=0
    g2: LineSegment StartX=-21.5 StartY=11.7 StartZ=0 EndX=-21.5 EndY=1 EndZ=0
    g3: LineSegment StartX=-21.5 StartY=1 StartZ=0 EndX=21.5 EndY=1 EndZ=0
    g4: LineSegment StartX=21.5 StartY=1 StartZ=0 EndX=21.5 EndY=11.7 EndZ=0
    g5: LineSegment StartX=21.5 StartY=11.7 StartZ=0 EndX=18.5 EndY=11.7 EndZ=0
    g6: LineSegment StartX=18.5 StartY=11.7 StartZ=0 EndX=18.5 EndY=12.7 EndZ=0
    g7: LineSegment StartX=18.5 StartY=12.7 StartZ=0 EndX=-18.5 EndY=12.7 EndZ=0
  constraints (23):
    c: Vertical(g0)
    c: Coincident(g0,g1)
    c: Horizontal(g1)
    c: Coincident(g1,g2)
    c: Vertical(g2)
    c: Coincident(g2,g3)
    c: Coincident(g3,g4)
    c: Vertical(g4)
    c: Coincident(g4,g5)
    c: Horizontal(g5)
    c: Coincident(g5,g6)
    c: Coincident(g6,g7)
    c: Coincident(g7,g0)
    c: PointOnObject(g6,g-4)
    c: DistanceX(g3,g-3) = 1
    c: DistanceY(g-3,g3) = 1
    c: DistanceY(g4,g-4) = 1
    c: Vertical(g6)
    c: Equal(g6,g0)
    c: Equal(g1,g5)
    c: Equal(g4,g2)
    c: Distance(g5) = 3
    c: Symmetric(g2,g3,g-2)
FEATURE [PartDesign::Pocket] Pocket
  BaseFeature = -> Pad
  ClaimChildren = false
  Length = 5
  Length2 = 100
  Placement = pos=(0,0,0) rot=(1,0,0;1.5708rad)
  Profile = -> Sketch001
  Type = 1
FEATURE [Sketcher::SketchObject] Sketch002
  MapMode = 5
  Placement = pos=(0,0,0) rot=(1,0,0;1.5708rad)
  Support = -> [XZ_Plane001]
  sketch-geometry (4):
    g0: LineSegment StartX=-17.5 StartY=12.7 StartZ=0 EndX=17.5 EndY=12.7 EndZ=0
    g1: LineSegment StartX=17.5 StartY=12.7 StartZ=0 EndX=17.5 EndY=2.7 EndZ=0
    g2: LineSegment StartX=17.5 StartY=2.7 StartZ=0 EndX=-17.5 EndY=2.7 EndZ=0
    g3: LineSegment StartX=-17.5 StartY=2.7 StartZ=0 EndX=-17.5 EndY=12.7 EndZ=0
  constraints (11):
    c: Coincident(g0,g1)
    c: Coincident(g1,g2)
    c: Coincident(g2,g3)
    c: Coincident(g3,g0)
    c: Horizontal(g2)
    c: Vertical(g1)
    c: Vertical(g3)
    c: Symmetric(g0,g0,g-2)
    c: Distance(g0) = 35
    c: DistanceY(g-1,g2) = 2.7
    c: Distance(g3) = 10
FEATURE [PartDesign::Pad] Pad001
  ClaimChildren = false
  Length = 450
  Length2 = 100
  Placement = pos=(0,0,0) rot=(1,0,0;1.5708rad)
  Profile = -> Sketch002
  Type = 0
FEATURE [Sketcher::SketchObject] Sketch003
  ExternalGeometry = -> [Pad001]
  MapMode = 5
  Placement = pos=(0,-450,-9.9e-14) rot=(1,0,0;1.5708rad)
  Support = -> [Pad001]
  sketch-geometry (8):
    g0: LineSegment StartX=-13.5 StartY=12.7 StartZ=0 EndX=-13.5 EndY=11.7 EndZ=0
    g1: LineSegment StartX=-13.5 StartY=11.7 StartZ=0 EndX=-16.5 EndY=11.7 EndZ=0
    g2: LineSegment StartX=-16.5 StartY=11.7 StartZ=0 EndX=-16.5 EndY=3.7 EndZ=0
    g3: LineSegment StartX=-16.5 StartY=3.7 StartZ=0 EndX=16.5 EndY=3.7 EndZ=0
    g4: LineSegment StartX=16.5 StartY=3.7 StartZ=0 EndX=16.5 EndY=11.7 EndZ=0
    g5: LineSegment StartX=16.5 StartY=11.7 StartZ=0 EndX=13.5 EndY=11.7 EndZ=0
    g6: LineSegment StartX=13.5 StartY=11.7 StartZ=0 EndX=13.5 EndY=12.7 EndZ=0
    g7: LineSegment StartX=13.5 StartY=12.7 StartZ=0 EndX=-13.5 EndY=12.7 EndZ=0
  constraints (23):
    c: PointOnObject(g0,g-3)
    c: Vertical(g0)
    c: Coincident(g0,g1)
    c: Horizontal(g1)
    c: Coincident(g1,g2)
    c: Vertical(g2)
    c: Coincident(g2,g3)
    c: Coincident(g3,g4)
    c: Vertical(g4)
    c: Coincident(g4,g5)
    c: Horizontal(g5)
    c: Coincident(g5,g6)
    c: PointOnObject(g6,g-3)
    c: Vertical(g6)
    c: Coincident(g6,g7)
    c: Coincident(g7,g0)
    c: Equal(g0,g6)
    c: Symmetric(g3,g2,g-2)
    c: Equal(g5,g1)
    c: DistanceX(g3,g-4) = 1
    c: DistanceY(g-4,g3) = 1
    c: DistanceY(g4,g-3) = 1
    c: Distance(g5) = 3
FEATURE [PartDesign::Pocket] Pocket001
  BaseFeature = -> Pad001
  ClaimChildren = false
  Length = 5
  Length2 = 100
  Placement = pos=(0,0,0) rot=(1,0,0;1.5708rad)
  Profile = -> Sketch003
  Type = 1
FEATURE [PartDesign::Body] Body001  label="rail 2"
  Group = -> [Sketch002,Pad001,Sketch003,Pocket001]
  Origin = -> Origin001
  SingleSolid = true
  Tip = -> Pocket001
FEATURE [Sketcher::SketchObject] Sketch004
  MapMode = 5
  Placement = pos=(0,0,0) rot=(1,0,0;1.5708rad)
  Support = -> [XZ_Plane002]
  sketch-geometry (4):
    g0: LineSegment StartX=-12.5 StartY=12.7 StartZ=0 EndX=12.5 EndY=12.7 EndZ=0
    g1: LineSegment StartX=12.5 StartY=12.7 StartZ=0 EndX=12.5 EndY=5.7 EndZ=0
    g2: LineSegment StartX=12.5 StartY=5.7 StartZ=0 EndX=-12.5 EndY=5.7 EndZ=0
    g3: LineSegment StartX=-12.5 StartY=5.7 StartZ=0 EndX=-12.5 EndY=12.7 EndZ=0
  constraints (11):
    c: Coincident(g0,g1)
    c: Coincident(g1,g2)
    c: Coincident(g2,g3)
    c: Coincident(g3,g0)
    c: Horizontal(g2)
    c: Vertical(g1)
    c: Vertical(g3)
    c: Symmetric(g0,g0,g-2)
    c: Distance(g0) = 25
    c: Distance(g3) = 7
    c: DistanceY(g-1,g0) = 12.7
FEATURE [PartDesign::Pad] Pad002
  ClaimChildren = false
  Length = 450
  Length2 = 100
  Placement = pos=(0,0,0) rot=(1,0,0;1.5708rad)
  Profile = -> Sketch004
  Type = 0
FEATURE [Sketcher::SketchObject] Sketch005
  ExternalGeometry = -> [Pad002]
  MapMode = 5
  Placement = pos=(0,-450,-9.9e-14) rot=(1,0,0;1.5708rad)
  Support = -> [Pad002]
  sketch-geometry (8):
    g0: LineSegment StartX=-11.5 StartY=11.7 StartZ=0 EndX=11.5 EndY=11.7 EndZ=0
    g1: LineSegment StartX=11.5 StartY=11.7 StartZ=0 EndX=11.5 EndY=6.7 EndZ=0
    g2: LineSegment StartX=11.5 StartY=6.7 StartZ=0 EndX=8.5 EndY=6.7 EndZ=0
    g3: LineSegment StartX=8.5 StartY=6.7 StartZ=0 EndX=8.5 EndY=5.7 EndZ=0
    g4: LineSegment StartX=8.5 StartY=5.7 StartZ=0 EndX=-8.5 EndY=5.7 EndZ=0
    g5: LineSegment StartX=-8.5 StartY=5.7 StartZ=0 EndX=-8.5 EndY=6.7 EndZ=0
    g6: LineSegment StartX=-8.5 StartY=6.7 StartZ=0 EndX=-11.5 EndY=6.7 EndZ=0
    g7: LineSegment StartX=-11.5 StartY=6.7 StartZ=0 EndX=-11.5 EndY=11.7 EndZ=0
  constraints (23):
    c: Coincident(g0,g1)
    c: Vertical(g1)
    c: Coincident(g1,g2)
    c: Horizontal(g2)
    c: Coincident(g2,g3)
    c: Vertical(g3)
    c: Coincident(g3,g4)
    c: Horizontal(g4)
    c: Coincident(g4,g5)
    c: Vertical(g5)
    c: Coincident(g5,g6)
    c: Horizontal(g6)
    c: Coincident(g6,g7)
    c: Coincident(g7,g0)
    c: Vertical(g7)
    c: PointOnObject(g4,g-3)
    c: Equal(g3,g5)
    c: Equal(g2,g6)
    c: DistanceX(g1,g-3) = 1
    c: DistanceY(g-3,g1) = 1
    c: Symmetric(g0,g0,g-2)
    c: Distance(g1) = 5
    c: Distance(g2) = 3
FEATURE [PartDesign::Pocket] Pocket002
  BaseFeature = -> Pad002
  ClaimChildren = false
  Length = 5
  Length2 = 100
  Placement = pos=(0,0,0) rot=(1,0,0;1.5708rad)
  Profile = -> Sketch005
  Type = 1
FEATURE [Sketcher::SketchObject] Sketch009
  MapMode = 5
  Placement = pos=(0,0,1) rot=(0,0,1;3.14159rad)
  Support = -> [Pocket]
  sketch-geometry (12):
    g0: LineSegment StartX=11 StartY=57 StartZ=0 EndX=11 EndY=26.2 EndZ=0
    g1: ArcOfCircle CenterX=8.8 CenterY=26.2 CenterZ=0 NormalX=0 NormalY=0 NormalZ=1 AngleXU=0 Radius=2.2 StartAngle=4.71239 EndAngle=6.28319
    g2: LineSegment StartX=8.8 StartY=24 StartZ=0 EndX=-8.8 EndY=24 EndZ=0
    g3: ArcOfCircle CenterX=-8.8 CenterY=26.2 CenterZ=0 NormalX=0 NormalY=0 NormalZ=1 AngleXU=0 Radius=2.2 StartAngle=3.14159 EndAngle=4.71239
    g4: LineSegment StartX=-11 StartY=26.2 StartZ=0 EndX=-11 EndY=57 EndZ=0
    g5: ArcOfCircle CenterX=-9.3 CenterY=57 CenterZ=0 NormalX=0 NormalY=0 NormalZ=1 AngleXU=0 Radius=1.7 StartAngle=-1.8e-15 EndAngle=3.14159
    g6: LineSegment StartX=-7.6 StartY=57 StartZ=0 EndX=-7.6 EndY=30.1 EndZ=0
    g7: ArcOfCircle CenterX=-5.9 CenterY=30.1 CenterZ=0 NormalX=0 NormalY=0 NormalZ=1 AngleXU=0 Radius=1.7 StartAngle=3.14159 EndAngle=4.71239
    g8: LineSegment StartX=-5.9 StartY=28.4 StartZ=0 EndX=5.9 EndY=28.4 EndZ=0
    g9: ArcOfCircle CenterX=5.9 CenterY=30.1 CenterZ=0 NormalX=0 NormalY=0 NormalZ=1 AngleXU=0 Radius=1.7 StartAngle=4.71239 EndAngle=6.28319
    g10: LineSegment StartX=7.6 StartY=30.1 StartZ=0 EndX=7.6 EndY=57 EndZ=0
    g11: ArcOfCircle CenterX=9.3 CenterY=57 CenterZ=0 NormalX=0 NormalY=0 NormalZ=1 AngleXU=0 Radius=1.7 StartAngle=-1.8e-15 EndAngle=3.14159
  constraints (30):
    c: Vertical(g0)
    c: Tangent(g0,g1) = 1.5708
    c: Tangent(g1,g2) = 1.5708
    c: Tangent(g2,g3) = 1.5708
    c: Tangent(g3,g4) = 1.5708
    c: Tangent(g4,g5) = 1.5708
    c: Tangent(g5,g6) = 1.5708
    c: Tangent(g6,g7) = -1.5708
    c: Tangent(g7,g8) = -1.5708
    c: Tangent(g8,g9) = -1.5708
    c: Tangent(g9,g10) = -1.5708
    c: Tangent(g10,g11) = 1.5708
    c: Horizontal(g8)
    c: Vertical(g10)
    c: Vertical(g6)
    c: Coincident(g11,g0)
    c: Vertical(g4)
    c: Equal(g6,g10)
    c: Equal(g4,g0)
    c: Horizontal(g10,g0)
    c: Equal(g5,g11)
    c: Equal(g9,g7)
    c: Diameter(g11) = 3.4
    c: Diameter(g1) = 4.4
    c: Diameter(g9) = 3.4
    c: DistanceY(g2,g7) = 4.4
    c: Symmetric(g1,g2,g-2)
    c: DistanceX(g3,g0) = 22
    c: DistanceY(g1,g10) = 33
    c: DistanceY(g-1,g2) = 24
FEATURE [PartDesign::Pocket] Pocket003
  BaseFeature = -> Pocket
  ClaimChildren = false
  Length = 5
  Length2 = 100
  Placement = pos=(0,0,0) rot=(1,0,0;1.5708rad)
  Profile = -> Sketch009
  Type = 1
FEATURE [PartDesign::LinearPattern] LinearPattern
  BaseFeature = -> Pocket003
  CopyShape = true
  Direction = -> Y_Axis
  Length = 65
  Occurrences = 2
  OriginalSubs = -> [Pocket003]
  Originals = -> [Pocket003]
  Placement = pos=(0,0,0) rot=(1,0,0;1.5708rad)
  Reversed = true
  SubTransform = true
FEATURE [PartDesign::LinearPattern] LinearPattern001
  BaseFeature = -> LinearPattern
  CopyShape = true
  Direction = -> Y_Axis
  Length = 320
  Occurrences = 3
  OriginalSubs = -> [Pocket003]
  Originals = -> [Pocket003]
  Placement = pos=(0,0,0) rot=(1,0,0;1.5708rad)
  Reversed = true
  SubTransform = true
FEATURE [PartDesign::LinearPattern] LinearPattern002
  BaseFeature = -> LinearPattern001
  CopyShape = true
  Direction = -> Y_Axis
  Length = 257
  Occurrences = 2
  OriginalSubs = -> [Pocket003]
  Originals = -> [Pocket003]
  Placement = pos=(0,0,0) rot=(1,0,0;1.5708rad)
  Reversed = true
  SubTransform = true
FEATURE [Sketcher::SketchObject] Sketch010
  ExternalGeometry = -> [LinearPattern002]
  MapMode = 5
  Placement = pos=(0,0,1) rot=(0,0,1;3.14159rad)
  Support = -> [LinearPattern002]
  sketch-geometry (57):
    g0: Circle CenterX=0 CenterY=6 CenterZ=0 NormalX=0 NormalY=0 NormalZ=1 AngleXU=0 Radius=2.4
    g1: Circle CenterX=0 CenterY=430 CenterZ=0 NormalX=0 NormalY=0 NormalZ=1 AngleXU=0 Radius=2.4
    g2: Circle CenterX=0 CenterY=35.1 CenterZ=0 NormalX=0 NormalY=0 NormalZ=1 AngleXU=0 Radius=2.2
    g3: Circle CenterX=0 CenterY=100.1 CenterZ=0 NormalX=0 NormalY=0 NormalZ=1 AngleXU=0 Radius=2.2
    g4: Circle CenterX=0 CenterY=195.1 CenterZ=0 NormalX=0 NormalY=0 NormalZ=1 AngleXU=0 Radius=2.2
    g5: Circle CenterX=0 CenterY=292.1 CenterZ=0 NormalX=0 NormalY=0 NormalZ=1 AngleXU=0 Radius=2.2
    g6: Circle CenterX=0 CenterY=355.1 CenterZ=0 NormalX=0 NormalY=0 NormalZ=1 AngleXU=0 Radius=2.2
    g7: Circle CenterX=0 CenterY=272.4 CenterZ=0 NormalX=0 NormalY=0 NormalZ=1 AngleXU=0 Radius=2.2
    g8: Circle CenterX=0 CenterY=179.4 CenterZ=0 NormalX=0 NormalY=0 NormalZ=1 AngleXU=0 Radius=2.2
    g9: ArcOfCircle CenterX=0 CenterY=48.8 CenterZ=0 NormalX=0 NormalY=0 NormalZ=1 AngleXU=0 Radius=2.2 StartAngle=3.14159 EndAngle=6.28319
    g10: ArcOfCircle CenterX=-2e-16 CenterY=53.2 CenterZ=0 NormalX=0 NormalY=0 NormalZ=1 AngleXU=0 Radius=2.2 StartAngle=-9e-16 EndAngle=3.14159
    g11: LineSegment StartX=2.2 StartY=48.8 StartZ=0 EndX=2.2 EndY=53.2 EndZ=0
    g12: LineSegment StartX=-2.2 StartY=48.8 StartZ=0 EndX=-2.2 EndY=53.2 EndZ=0
    g13: ArcOfCircle CenterX=0 CenterY=64.8 CenterZ=0 NormalX=0 NormalY=0 NormalZ=1 AngleXU=0 Radius=2.2 StartAngle=3.14159 EndAngle=6.28319
    g14: ArcOfCircle CenterX=0 CenterY=69.2 CenterZ=0 NormalX=0 NormalY=0 NormalZ=1 AngleXU=0 Radius=2.2 StartAngle=1.2e-15 EndAngle=3.14159
    g15: LineSegment StartX=2.2 StartY=64.8 StartZ=0 EndX=2.2 EndY=69.2 EndZ=0
    g16: LineSegment StartX=-2.2 StartY=64.8 StartZ=0 EndX=-2.2 EndY=69.2 EndZ=0
    g17: ArcOfCircle CenterX=0 CenterY=113.8 CenterZ=0 NormalX=0 NormalY=0 NormalZ=1 AngleXU=0 Radius=2.2 StartAngle=3.14159 EndAngle=6.28319
    g18: ArcOfCircle CenterX=2e-16 CenterY=118.2 CenterZ=0 NormalX=0 NormalY=0 NormalZ=1 AngleXU=0 Radius=2.2 StartAngle=9e-16 EndAngle=3.14159
    g19: LineSegment StartX=2.2 StartY=113.8 StartZ=0 EndX=2.2 EndY=118.2 EndZ=0
    g20: LineSegment StartX=-2.2 StartY=113.8 StartZ=0 EndX=-2.2 EndY=118.2 EndZ=0
    g21: ArcOfCircle CenterX=0 CenterY=129.8 CenterZ=0 NormalX=0 NormalY=0 NormalZ=1 AngleXU=0 Radius=2.2 StartAngle=3.14159 EndAngle=6.28319
    g22: ArcOfCircle CenterX=1e-16 CenterY=134.2 CenterZ=0 NormalX=0 NormalY=0 NormalZ=1 AngleXU=0 Radius=2.2 StartAngle=0 EndAngle=3.14159
    g23: LineSegment StartX=2.2 StartY=129.8 StartZ=0 EndX=2.2 EndY=134.2 EndZ=0
    g24: LineSegment StartX=-2.2 StartY=129.8 StartZ=0 EndX=-2.2 EndY=134.2 EndZ=0
    g25: ArcOfCircle CenterX=0 CenterY=208.8 CenterZ=0 NormalX=0 NormalY=0 NormalZ=1 AngleXU=0 Radius=2.2 StartAngle=3.14159 EndAngle=6.28319
    g26: ArcOfCircle CenterX=2e-16 CenterY=213.2 CenterZ=0 NormalX=0 NormalY=0 NormalZ=1 AngleXU=0 Radius=2.2 StartAngle=-4.4e-15 EndAngle=3.14159
    g27: LineSegment StartX=2.2 StartY=208.8 StartZ=0 EndX=2.2 EndY=213.2 EndZ=0
    g28: LineSegment StartX=-2.2 StartY=208.8 StartZ=0 EndX=-2.2 EndY=213.2 EndZ=0
    g29: ArcOfCircle CenterX=0 CenterY=224.8 CenterZ=0 NormalX=0 NormalY=0 NormalZ=1 AngleXU=0 Radius=2.2 StartAngle=3.14159 EndAngle=6.28319
    g30: ArcOfCircle CenterX=0 CenterY=229.2 CenterZ=0 NormalX=0 NormalY=0 NormalZ=1 AngleXU=0 Radius=2.2 StartAngle=1.1e-15 EndAngle=3.14159
    g31: LineSegment StartX=2.2 StartY=224.8 StartZ=0 EndX=2.2 EndY=229.2 EndZ=0
    g32: LineSegment StartX=-2.2 StartY=224.8 StartZ=0 EndX=-2.2 EndY=229.2 EndZ=0
    g33: ArcOfCircle CenterX=0 CenterY=305.8 CenterZ=0 NormalX=0 NormalY=0 NormalZ=1 AngleXU=0 Radius=2.2 StartAngle=3.14159 EndAngle=6.28319
    g34: ArcOfCircle CenterX=-1e-16 CenterY=310.2 CenterZ=0 NormalX=0 NormalY=0 NormalZ=1 AngleXU=0 Radius=2.2 StartAngle=-1.15e-14 EndAngle=3.14159
    g35: LineSegment StartX=2.2 StartY=305.8 StartZ=0 EndX=2.2 EndY=310.2 EndZ=0
    g36: LineSegment StartX=-2.2 StartY=305.8 StartZ=0 EndX=-2.2 EndY=310.2 EndZ=0
    g37: ArcOfCircle CenterX=0 CenterY=321.8 CenterZ=0 NormalX=0 NormalY=0 NormalZ=1 AngleXU=0 Radius=2.2 StartAngle=3.14159 EndAngle=6.28319
    g38: ArcOfCircle CenterX=-1e-16 CenterY=326.2 CenterZ=0 NormalX=0 NormalY=0 NormalZ=1 AngleXU=0 Radius=2.2 StartAngle=-9e-16 EndAngle=3.14159
    g39: LineSegment StartX=2.2 StartY=321.8 StartZ=0 EndX=2.2 EndY=326.2 EndZ=0
    g40: LineSegment StartX=-2.2 StartY=321.8 StartZ=0 EndX=-2.2 EndY=326.2 EndZ=0
    g41: ArcOfCircle CenterX=0 CenterY=368.8 CenterZ=0 NormalX=0 NormalY=0 NormalZ=1 AngleXU=0 Radius=2.2 StartAngle=3.14159 EndAngle=6.28319
    g42: ArcOfCircle CenterX=-2.4482e-12 CenterY=373.2 CenterZ=0 NormalX=0 NormalY=0 NormalZ=1 AngleXU=0 Radius=2.2 StartAngle=-4.254e-13 EndAngle=3.14159
    g43: LineSegment StartX=2.2 StartY=368.8 StartZ=0 EndX=2.2 EndY=373.2 EndZ=0
    g44: LineSegment StartX=-2.2 StartY=368.8 StartZ=0 EndX=-2.2 EndY=373.2 EndZ=0
    g45: ArcOfCircle CenterX=0 CenterY=384.8 CenterZ=0 NormalX=0 NormalY=0 NormalZ=1 AngleXU=0 Radius=2.2 StartAngle=3.14159 EndAngle=6.28319
    g46: ArcOfCircle CenterX=2.4481e-12 CenterY=389.2 CenterZ=0 NormalX=0 NormalY=0 NormalZ=1 AngleXU=0 Radius=2.2 StartAngle=-2.7e-15 EndAngle=3.14159
    g47: LineSegment StartX=2.2 StartY=384.8 StartZ=0 EndX=2.2 EndY=389.2 EndZ=0
    g48: LineSegment StartX=-2.2 StartY=384.8 StartZ=0 EndX=-2.2 EndY=389.2 EndZ=0
    g49: LineSegment StartX=21 StartY=4 StartZ=0 EndX=16 EndY=4 EndZ=0
    g50: LineSegment StartX=16 StartY=4 StartZ=0 EndX=16 EndY=8 EndZ=0
    g51: LineSegment StartX=16 StartY=8 StartZ=0 EndX=21 EndY=8 EndZ=0
    g52: LineSegment StartX=21 StartY=8 StartZ=0 EndX=21 EndY=4 EndZ=0
    g53: LineSegment StartX=-16 StartY=4 StartZ=0 EndX=-21 EndY=4 EndZ=0
    g54: LineSegment StartX=-21 StartY=4 StartZ=0 EndX=-21 EndY=8 EndZ=0
    g55: LineSegment StartX=-21 StartY=8 StartZ=0 EndX=-16 EndY=8 EndZ=0
    g56: LineSegment StartX=-16 StartY=8 StartZ=0 EndX=-16 EndY=4 EndZ=0
  constraints (150):
    c: PointOnObject(g0,g-2)
    c: Equal(g1,g0)
    c: Diameter(g0) = 4.8
    c: DistanceY(g-1,g0) = 6
    c: DistanceY(g-1,g1) = 430
    c: PointOnObject(g1,g-2)
    c: PointOnObject(g2,g-2)
    c: PointOnObject(g3,g-2)
    c: PointOnObject(g4,g-2)
    c: PointOnObject(g5,g-2)
    c: PointOnObject(g6,g-2)
    c: PointOnObject(g7,g-2)
    c: PointOnObject(g8,g-2)
    c: Equal(g3,g8)
    c: Equal(g8,g4)
    c: Equal(g4,g7)
    c: Equal(g7,g5)
    c: Equal(g5,g6)
    c: Diameter(g2) = 4.4
    c: DistanceY(g-7,g6) = 6.7
    c: DistanceY(g-6,g5) = 6.7
    c: DistanceY(g-5,g4) = 6.7
    c: DistanceY(g-4,g3) = 6.7
    c: DistanceY(g-3,g2) = 6.7
    c: Equal(g2,g3)
    c: DistanceY(g7,g-6) = 13
    c: DistanceY(g8,g-5) = 9
    c: Tangent(g9,g12) = 1.5708
    c: Tangent(g9,g11) = -1.5708
    c: Tangent(g11,g10) = -1.5708
    c: Tangent(g12,g10) = 1.5708
    c: Vertical(g11)
    c: Equal(g9,g10)
    c: PointOnObject(g9,g-2)
    c: Diameter(g9) = 4.4
    c: Distance(g12) = 4.4
    c: DistanceY(g-3,g9) = 20.4
    c: Tangent(g13,g16) = 1.5708
    c: Tangent(g13,g15) = -1.5708
    c: Tangent(g15,g14) = -1.5708
    c: Tangent(g16,g14) = 1.5708
    c: Vertical(g15)
    c: Equal(g13,g14)
    c: PointOnObject(g13,g-2)
    c: Equal(g12,g16)
    c: Equal(g13,g10)
    c: DistanceY(g10,g13) = 11.6
    c: Tangent(g17,g20) = 1.5708
    c: Tangent(g17,g19) = -1.5708
    c: Tangent(g19,g18) = -1.5708
    c: Tangent(g20,g18) = 1.5708
    c: Vertical(g19)
    c: Equal(g17,g18)
    c: PointOnObject(g17,g-2)
    c: Equal(g20,g16)
    c: Equal(g17,g13)
    c: DistanceY(g-4,g17) = 20.4
    c: Tangent(g21,g24) = 1.5708
    c: Tangent(g21,g23) = -1.5708
    c: Tangent(g23,g22) = -1.5708
    c: Tangent(g24,g22) = 1.5708
    c: Vertical(g23)
    c: Equal(g21,g22)
    c: PointOnObject(g21,g-2)
    c: Equal(g24,g20)
    c: Equal(g17,g21)
    c: DistanceY(g18,g21) = 11.6
    c: Tangent(g25,g28) = 1.5708
    c: Tangent(g25,g27) = -1.5708
    c: Tangent(g27,g26) = -1.5708
    c: Tangent(g28,g26) = 1.5708
    c: Vertical(g27)
    c: Equal(g25,g26)
    c: PointOnObject(g25,g-2)
    c: Equal(g28,g24)
    c: Equal(g25,g21)
    c: DistanceY(g-5,g25) = 20.4
    c: Tangent(g29,g32) = 1.5708
    c: Tangent(g29,g31) = -1.5708
    c: Tangent(g31,g30) = -1.5708
    c: Tangent(g32,g30) = 1.5708
    c: Vertical(g31)
    c: Equal(g29,g30)
    c: PointOnObject(g29,g-2)
    c: Equal(g32,g28)
    c: Equal(g29,g25)
    c: DistanceY(g26,g29) = 11.6
    c: Tangent(g33,g36) = 1.5708
    c: Tangent(g33,g35) = -1.5708
    c: Tangent(g35,g34) = -1.5708
    c: Tangent(g36,g34) = 1.5708
    c: Vertical(g35)
    c: Equal(g33,g34)
    c: PointOnObject(g33,g-2)
    c: Equal(g32,g36)
    c: Equal(g33,g30)
    c: DistanceY(g-6,g33) = 20.4
    c: Tangent(g37,g40) = 1.5708
    c: Tangent(g37,g39) = -1.5708
    c: Tangent(g39,g38) = -1.5708
    c: Tangent(g40,g38) = 1.5708
    c: Vertical(g39)
    c: Equal(g37,g38)
    c: PointOnObject(g37,g-2)
    c: Equal(g40,g36)
    c: Equal(g37,g34)
    c: DistanceY(g34,g37) = 11.6
    c: Tangent(g41,g44) = 1.5708
    c: Tangent(g41,g43) = -1.5708
    c: Tangent(g43,g42) = -1.5708
    c: Tangent(g44,g42) = 1.5708
    c: Vertical(g43)
    c: Equal(g41,g42)
    c: PointOnObject(g41,g-2)
    c: Equal(g44,g40)
    c: Equal(g41,g38)
    c: DistanceY(g-7,g41) = 20.4
    c: Tangent(g45,g48) = 1.5708
    c: Tangent(g45,g47) = -1.5708
    c: Tangent(g47,g46) = -1.5708
    c: Tangent(g48,g46) = 1.5708
    c: Vertical(g47)
    c: Equal(g45,g46)
    c: PointOnObject(g45,g-2)
    c: Equal(g48,g44)
    c: Equal(g45,g42)
    c: DistanceY(g42,g45) = 11.6
    c: Coincident(g49,g50)
    c: Coincident(g50,g51)
    c: Coincident(g51,g52)
    c: Coincident(g52,g49)
    c: Horizontal(g49)
    c: Horizontal(g51)
    c: Vertical(g50)
    c: Vertical(g52)
    c: Coincident(g53,g54)
    c: Coincident(g54,g55)
    c: Coincident(g55,g56)
    c: Coincident(g56,g53)
    c: Horizontal(g53)
    c: Horizontal(g55)
    c: Vertical(g54)
    c: Vertical(g56)
    c: Equal(g56,g50)
    c: Equal(g53,g49)
    c: Symmetric(g53,g49,g-2)
    c: Distance(g54) = 4
    c: Distance(g53) = 5
    c: DistanceY(g-1,g53) = 4
    c: DistanceX(g53,g-1) = 21
FEATURE [PartDesign::Pocket] Pocket004
  BaseFeature = -> LinearPattern002
  ClaimChildren = false
  Length = 5
  Length2 = 100
  Placement = pos=(0,0,0) rot=(1,0,0;1.5708rad)
  Profile = -> Sketch010
  Type = 1
FEATURE [Sketcher::SketchObject] Sketch011
  MapMode = 5
  Placement = pos=(0,0,12.7) rot=(0,0,1;3.14159rad)
  Support = -> [Pocket002]
  sketch-geometry (36):
    g0: Circle CenterX=0 CenterY=25 CenterZ=0 NormalX=0 NormalY=0 NormalZ=1 AngleXU=0 Radius=2.2
    g1: ArcOfCircle CenterX=2.2 CenterY=35 CenterZ=0 NormalX=0 NormalY=0 NormalZ=1 AngleXU=0 Radius=2.2 StartAngle=4.71239 EndAngle=7.85398
    g2: ArcOfCircle CenterX=-2.2 CenterY=35 CenterZ=0 NormalX=0 NormalY=0 NormalZ=1 AngleXU=0 Radius=2.2 StartAngle=1.5708 EndAngle=4.71239
    g3: LineSegment StartX=2.2 StartY=37.2 StartZ=0 EndX=-2.2 EndY=37.2 EndZ=0
    g4: LineSegment StartX=2.2 StartY=32.8 StartZ=0 EndX=-2.2 EndY=32.8 EndZ=0
    g5: ArcOfCircle CenterX=0 CenterY=50 CenterZ=0 NormalX=0 NormalY=0 NormalZ=1 AngleXU=0 Radius=2.2 StartAngle=-9e-16 EndAngle=3.14159
    g6: ArcOfCircle CenterX=-2e-16 CenterY=45.6 CenterZ=0 NormalX=0 NormalY=0 NormalZ=1 AngleXU=0 Radius=2.2 StartAngle=3.14159 EndAngle=6.28319
    g7: LineSegment StartX=-2.2 StartY=50 StartZ=0 EndX=-2.2 EndY=45.6 EndZ=0
    g8: LineSegment StartX=2.2 StartY=50 StartZ=0 EndX=2.2 EndY=45.6 EndZ=0
    g9: Circle CenterX=0 CenterY=185 CenterZ=0 NormalX=0 NormalY=0 NormalZ=1 AngleXU=0 Radius=2.2
    g10: ArcOfCircle CenterX=2.2 CenterY=195 CenterZ=0 NormalX=0 NormalY=0 NormalZ=1 AngleXU=0 Radius=2.2 StartAngle=4.71239 EndAngle=7.85398
    g11: ArcOfCircle CenterX=-2.2 CenterY=195 CenterZ=0 NormalX=0 NormalY=0 NormalZ=1 AngleXU=0 Radius=2.2 StartAngle=1.5708 EndAngle=4.71239
    g12: LineSegment StartX=2.2 StartY=197.2 StartZ=0 EndX=-2.2 EndY=197.2 EndZ=0
    g13: LineSegment StartX=2.2 StartY=192.8 StartZ=0 EndX=-2.2 EndY=192.8 EndZ=0
    g14: ArcOfCircle CenterX=0 CenterY=205.6 CenterZ=0 NormalX=0 NormalY=0 NormalZ=1 AngleXU=0 Radius=2.2 StartAngle=3.14159 EndAngle=6.28319
    g15: ArcOfCircle CenterX=0 CenterY=210 CenterZ=0 NormalX=0 NormalY=0 NormalZ=1 AngleXU=0 Radius=2.2 StartAngle=2.8e-15 EndAngle=3.14159
    g16: LineSegment StartX=2.2 StartY=205.6 StartZ=0 EndX=2.2 EndY=210 EndZ=0
    g17: LineSegment StartX=-2.2 StartY=205.6 StartZ=0 EndX=-2.2 EndY=210 EndZ=0
    g18: LineSegment [constr] StartX=0 StartY=35 StartZ=0 EndX=0 EndY=25 EndZ=0
    g19: LineSegment [constr] StartX=2.2 StartY=35 StartZ=0 EndX=0 EndY=35 EndZ=0
    g20: LineSegment [constr] StartX=0 StartY=35 StartZ=0 EndX=-2e-16 EndY=45.6 EndZ=0
    g21: LineSegment [constr] StartX=2.2 StartY=195 StartZ=0 EndX=0 EndY=195 EndZ=0
    g22: LineSegment [constr] StartX=0 StartY=185 StartZ=0 EndX=0 EndY=195 EndZ=0
    g23: LineSegment [constr] StartX=0 StartY=195 StartZ=0 EndX=0 EndY=205.6 EndZ=0
    g24: Circle CenterX=0 CenterY=377 CenterZ=0 NormalX=0 NormalY=0 NormalZ=1 AngleXU=0 Radius=2.2
    g25: ArcOfCircle CenterX=2.2 CenterY=387 CenterZ=0 NormalX=0 NormalY=0 NormalZ=1 AngleXU=0 Radius=2.2 StartAngle=4.71239 EndAngle=7.85398
    g26: ArcOfCircle CenterX=-2.2 CenterY=387 CenterZ=0 NormalX=0 NormalY=0 NormalZ=1 AngleXU=0 Radius=2.2 StartAngle=1.5708 EndAngle=4.71239
    g27: LineSegment StartX=2.2 StartY=389.2 StartZ=0 EndX=-2.2 EndY=389.2 EndZ=0
    g28: LineSegment StartX=2.2 StartY=384.8 StartZ=0 EndX=-2.2 EndY=384.8 EndZ=0
    g29: ArcOfCircle CenterX=0 CenterY=402 CenterZ=0 NormalX=0 NormalY=0 NormalZ=1 AngleXU=0 Radius=2.2 StartAngle=-7.1e-15 EndAngle=3.14159
    g30: ArcOfCircle CenterX=-1e-16 CenterY=397.6 CenterZ=0 NormalX=0 NormalY=0 NormalZ=1 AngleXU=0 Radius=2.2 StartAngle=3.14159 EndAngle=6.28319
    g31: LineSegment StartX=-2.2 StartY=402 StartZ=0 EndX=-2.2 EndY=397.6 EndZ=0
    g32: LineSegment StartX=2.2 StartY=402 StartZ=0 EndX=2.2 EndY=397.6 EndZ=0
    g33: LineSegment [constr] StartX=2.2 StartY=387 StartZ=0 EndX=0 EndY=387 EndZ=0
    g34: LineSegment [constr] StartX=0 StartY=377 StartZ=0 EndX=0 EndY=387 EndZ=0
    g35: LineSegment [constr] StartX=0 StartY=387 StartZ=0 EndX=-1e-16 EndY=397.6 EndZ=0
  constraints (89):
    c: PointOnObject(g0,g-2)
    c: Tangent(g1,g4) = 1.5708
    c: Tangent(g1,g3) = -1.5708
    c: Tangent(g3,g2) = -1.5708
    c: Tangent(g4,g2) = 1.5708
    c: Horizontal(g3)
    c: Tangent(g5,g8) = 1.5708
    c: Tangent(g5,g7) = -1.5708
    c: Tangent(g7,g6) = -1.5708
    c: Tangent(g8,g6) = 1.5708
    c: Vertical(g7)
    c: Equal(g5,g6)
    c: PointOnObject(g5,g-2)
    c: Equal(g4,g8)
    c: Equal(g2,g5)
    c: Symmetric(g2,g1,g-2)
    c: Diameter(g2) = 4.4
    c: Distance(g4) = 4.4
    c: Diameter(g0) = 4.4
    c: DistanceY(g-1,g0) = 25
    c: DistanceY(g-1,g2) = 35
    c: DistanceY(g5) = 50
    c: PointOnObject(g9,g-2)
    c: Tangent(g10,g13) = 1.5708
    c: Tangent(g10,g12) = -1.5708
    c: Tangent(g12,g11) = -1.5708
    c: Tangent(g13,g11) = 1.5708
    c: Horizontal(g12)
    c: Tangent(g14,g17) = 1.5708
    c: Tangent(g14,g16) = -1.5708
    c: Tangent(g16,g15) = -1.5708
    c: Tangent(g17,g15) = 1.5708
    c: Vertical(g16)
    c: Equal(g14,g15)
    c: Equal(g14,g11)
    c: Equal(g11,g10)
    c: Equal(g15,g5)
    c: Equal(g9,g0)
    c: Equal(g7,g17)
    c: Equal(g13,g3)
    c: PointOnObject(g18,g-2)
    c: Coincident(g18,g0)
    c: Coincident(g19,g1)
    c: Horizontal(g19)
    c: Coincident(g19,g18)
    c: Coincident(g20,g18)
    c: Coincident(g20,g6)
    c: PointOnObject(g21,g-2)
    c: Coincident(g21,g10)
    c: Horizontal(g21)
    c: DistanceY(g0,g9) = 160
    c: Equal(g21,g19)
    c: Coincident(g22,g9)
    c: Coincident(g22,g21)
    c: Coincident(g23,g21)
    c: Coincident(g23,g14)
    c: Vertical(g23)
    c: Equal(g23,g20)
    c: Equal(g18,g22)
    c: PointOnObject(g24,g-2)
    c: Tangent(g25,g28) = 1.5708
    c: Tangent(g25,g27) = -1.5708
    c: Tangent(g27,g26) = -1.5708
    c: Tangent(g28,g26) = 1.5708
    c: Horizontal(g27)
    c: Equal(g25,g26)
    c: Tangent(g29,g32) = 1.5708
    c: Tangent(g29,g31) = -1.5708
    c: Tangent(g31,g30) = -1.5708
    c: Tangent(g32,g30) = 1.5708
    c: Vertical(g31)
    c: Equal(g29,g30)
    c: PointOnObject(g29,g-2)
    c: Equal(g30,g26)
    c: Equal(g26,g5)
    c: Equal(g24,g0)
    c: Equal(g28,g4)
    c: Equal(g7,g31)
    c: Coincident(g33,g25)
    c: PointOnObject(g33,g-2)
    c: Horizontal(g33)
    c: Coincident(g34,g24)
    c: Coincident(g34,g33)
    c: Coincident(g35,g33)
    c: Coincident(g35,g30)
    c: Equal(g34,g18)
    c: Equal(g20,g35)
    c: Equal(g33,g19)
    c: DistanceY(g0,g24) = 352
FEATURE [PartDesign::Pocket] Pocket005
  BaseFeature = -> Pocket002
  ClaimChildren = false
  Length = 5
  Length2 = 100
  Placement = pos=(0,0,0) rot=(1,0,0;1.5708rad)
  Profile = -> Sketch011
  Type = 1
FEATURE [App::FeaturePython] Constraints  # WARN: FeaturePython — macro-defined, semantics opaque (R4)
  GroupMode = 1
  _Version = 1
FEATURE [App::FeaturePython] Constraints001  # WARN: FeaturePython — macro-defined, semantics opaque (R4)
  GroupMode = 1
  _Version = 1
FEATURE [App::FeaturePython] Elements001  # WARN: FeaturePython — macro-defined, semantics opaque (R4)
  GroupMode = 1
FEATURE [Part::FeaturePython] Parts001  # WARN: FeaturePython — macro-defined, semantics opaque (R4)
  Group = -> [Origin004,Body001]
  GroupMode = 0
FEATURE [Part::FeaturePython] Assembly001  label="rail middle"  # WARN: FeaturePython — macro-defined, semantics opaque (R4)
  AutoRelax = true
  BuildShape = 0
  Freeze = false
  Group = -> [Constraints001,Elements001,Parts001]
  GroupMode = 1
  SolverType = 1
  Verbose = false
  _SolverType = 1
  _Version = 1
FEATURE [App::FeaturePython] Constraints002  # WARN: FeaturePython — macro-defined, semantics opaque (R4)
  GroupMode = 1
  _Version = 1
FEATURE [PartDesign::Line] DatumLine
  AttacherType = Attacher::AttachEngineLine
  AttachmentOffset = pos=(6.35,0,0) rot=(0,0,1;0rad)
  MapMode = 16
  Placement = pos=(-4e-16,4e-16,6.35) rot=(0.57735,0.57735,0.57735;4.18879rad)
  Support = -> [Y_Axis]
FEATURE [PartDesign::Body] Body  label="rail 1"
  Group = -> [Sketch,Pad,Sketch001,Pocket,Sketch009,Pocket003,LinearPattern,LinearPattern001,LinearPattern002,Sketch010,Pocket004,DatumLine]
  Origin = -> Origin
  SingleSolid = true
  Tip = -> Pocket004
FEATURE [Part::FeaturePython] Parts  # WARN: FeaturePython — macro-defined, semantics opaque (R4)
  Group = -> [Origin003,Body]
  GroupMode = 0
FEATURE [PartDesign::Line] DatumLine001
  AttacherType = Attacher::AttachEngineLine
  AttachmentOffset = pos=(6.35,0,0) rot=(0,0,1;0rad)
  MapMode = 16
  Placement = pos=(-4e-16,4e-16,6.35) rot=(0.57735,0.57735,0.57735;4.18879rad)
  Support = -> [Y_Axis002]
FEATURE [PartDesign::Body] Body002  label="rail 3"
  Group = -> [Sketch004,Pad002,Sketch005,Pocket002,Sketch011,Pocket005,DatumLine001]
  Origin = -> Origin002
  SingleSolid = true
  Tip = -> Pocket005
FEATURE [Part::FeaturePython] Parts002  # WARN: FeaturePython — macro-defined, semantics opaque (R4)
  Group = -> [Origin005,Body002]
  GroupMode = 0
FEATURE [Part::FeaturePython] Assembly  label="rail bottom"  # WARN: FeaturePython — macro-defined, semantics opaque (R4)
  AutoRelax = true
  BuildShape = 0
  Freeze = false
  Group = -> [Constraints,Elements,Parts]
  GroupMode = 1
  SolverType = 1
  Verbose = false
  _SolverType = 1
  _Version = 1
FEATURE [App::FeaturePython] Elements  # WARN: FeaturePython — macro-defined, semantics opaque (R4)
  Group = -> [Element003,Element004,Element005]
  GroupMode = 1
FEATURE [Part::FeaturePython] Assembly002  label="rail top"  # WARN: FeaturePython — macro-defined, semantics opaque (R4)
  AutoRelax = true
  BuildShape = 0
  Freeze = false
  Group = -> [Constraints002,Elements002,Parts002]
  GroupMode = 1
  SolverType = 1
  Verbose = false
  _SolverType = 1
  _Version = 1
FEATURE [App::FeaturePython] Elements002  # WARN: FeaturePython — macro-defined, semantics opaque (R4)
  Group = -> [Element,Element001,Element002,Element006]
  GroupMode = 1
FEATURE [Part::FeaturePython] Element  label="mount_top"  # link proxy (typed FeaturePython)
  Detach = false
  LinkTransform = true
  LinkedObject = -> Body002 [Pocket005.Sketch011.Edge1]
  _Parent = -> Elements002
FEATURE [Part::FeaturePython] Element001  label="mount_middle"  # link proxy (typed FeaturePython)
  Detach = false
  LinkTransform = true
  LinkedObject = -> Body002 [Pocket005.Sketch011.Edge10]
  _Parent = -> Elements002
FEATURE [Part::FeaturePython] Element002  label="mount_bottom"  # link proxy (typed FeaturePython)
  Detach = false
  LinkTransform = true
  LinkedObject = -> Body002 [Pocket005.Sketch011.Edge19]
  _Parent = -> Elements002
FEATURE [Part::FeaturePython] Element003  label="mount_top"  # link proxy (typed FeaturePython)
  Detach = false
  LinkTransform = true
  LinkedObject = -> Body [Pocket004.Sketch010.Edge1]
  _Parent = -> Elements
FEATURE [Part::FeaturePython] Element004  label="mount_bottom"  # link proxy (typed FeaturePython)
  Detach = false
  LinkTransform = true
  LinkedObject = -> Body [Pocket004.Sketch010.Edge2]
  _Parent = -> Elements
FEATURE [Part::FeaturePython] Element005  label="slide_axis"  # link proxy (typed FeaturePython)
  Detach = false
  LinkTransform = true
  LinkedObject = -> Body [DatumLine.]
  _Parent = -> Elements
FEATURE [Part::FeaturePython] Element006  label="slide_axis"  # link proxy (typed FeaturePython)
  Detach = false
  LinkTransform = true
  LinkedObject = -> Body002 [DatumLine001.]
  _Parent = -> Elements002
---- part ../parts/lift/middle-stage-actuator-rod.FCStd = doc fcstd_cc32772ce5a1 ----
FCSTD DOCUMENT  (FreeCAD 0.19R18044 (Git))
Label: middle-stage-actuator-rod
License: Public Domain
LicenseURL: http://en.wikipedia.org/wiki/Public_domain
objects: Part::FeaturePython×6, App::FeaturePython×2, Sketcher::SketchObject×1, PartDesign::Pad×1, PartDesign::Body×1
note: 9 computed .brp shape members not serialized (recipe doc carries the construction recipe); baked Part::Feature solids carry a one-line shape summary decoded from their .brp

FEATURE [App::FeaturePython] Constraints  # WARN: FeaturePython — macro-defined, semantics opaque (R4)
  GroupMode = 1
  _Version = 1
FEATURE [Sketcher::SketchObject] Sketch
  MapMode = 5
  Placement = pos=(0,0,0) rot=(0.57735,0.57735,0.57735;2.0944rad)
  Support = -> [YZ_Plane]
  sketch-geometry (1):
    g0: Circle CenterX=0 CenterY=0 CenterZ=0 NormalX=0 NormalY=0 NormalZ=1 AngleXU=0 Radius=3
  constraints (2):
    c: Coincident(g0,g-1)
    c: Radius(g0) = 3
FEATURE [PartDesign::Pad] Pad
  ClaimChildren = false
  Length = 186.6
  Length2 = 100
  Midplane = true
  Placement = pos=(0,0,0) rot=(0.57735,0.57735,0.57735;2.0944rad)
  Profile = -> Sketch
  Type = 0
FEATURE [PartDesign::Body] Body
  Group = -> [Sketch,Pad]
  Origin = -> Origin
  Tip = -> Pad
FEATURE [Part::FeaturePython] Parts  # WARN: FeaturePython — macro-defined, semantics opaque (R4)
  Group = -> [Origin001,Body]
  GroupMode = 0
FEATURE [Part::FeaturePython] Element  label="center"  # link proxy (typed FeaturePython)
  Detach = false
  LinkTransform = true
  LinkedObject = -> Body [Pad.Sketch.Edge1]
  _Parent = -> Elements
FEATURE [Part::FeaturePython] Element001  label="left"  # link proxy (typed FeaturePython)
  Detach = false
  LinkTransform = true
  LinkedObject = -> Body [Pad.Edge2]
  _Parent = -> Elements
FEATURE [Part::FeaturePython] Element002  label="right"  # link proxy (typed FeaturePython)
  Detach = false
  LinkTransform = true
  LinkedObject = -> Body [Pad.Edge3]
  _Parent = -> Elements
FEATURE [App::FeaturePython] Elements  # WARN: FeaturePython — macro-defined, semantics opaque (R4)
  Group = -> [Element,Element001,Element002,Element003]
  GroupMode = 1
FEATURE [Part::FeaturePython] Assembly  label="middle-stage-actuator-rod"  # WARN: FeaturePython — macro-defined, semantics opaque (R4)
  AutoRelax = true
  BuildShape = 0
  Freeze = false
  Group = -> [Constraints,Elements,Parts]
  GroupMode = 1
  SolverType = 1
  Verbose = false
  _SolverType = 1
  _Version = 1
FEATURE [Part::FeaturePython] Element003  # link proxy (typed FeaturePython)
  Detach = false
  LinkTransform = true
  LinkedObject = -> Body [Pad.Face1]
  _Parent = -> Elements
---- part ../parts/lift/middle-stage-beam.FCStd = doc fcstd_69fa58f6fd3b ----
FCSTD DOCUMENT  (FreeCAD 0.19R18044 (Git))
Label: middle-stage-beam
License: Public Domain
LicenseURL: http://en.wikipedia.org/wiki/Public_domain
objects: Part::FeaturePython×20, Sketcher::SketchObject×5, PartDesign::Pocket×4, App::FeaturePython×4, PartDesign::Pad×1, PartDesign::Body×1, Part::Mirroring×1
note: 35 computed .brp shape members not serialized (recipe doc carries the construction recipe); baked Part::Feature solids carry a one-line shape summary decoded from their .brp

FEATURE [Sketcher::SketchObject] Sketch
  MapMode = 5
  Support = -> [XY_Plane]
  sketch-geometry (4):
    g0: LineSegment StartX=-22 StartY=47 StartZ=0 EndX=22 EndY=47 EndZ=0
    g1: LineSegment StartX=22 StartY=47 StartZ=0 EndX=22 EndY=-47 EndZ=0
    g2: LineSegment StartX=22 StartY=-47 StartZ=0 EndX=-22 EndY=-47 EndZ=0
    g3: LineSegment StartX=-22 StartY=-47 StartZ=0 EndX=-22 EndY=47 EndZ=0
  constraints (10):
    c: Coincident(g0,g1)
    c: Coincident(g1,g2)
    c: Coincident(g2,g3)
    c: Coincident(g3,g0)
    c: Horizontal(g2)
    c: Vertical(g1)
    c: Symmetric(g0,g2,g-1)
    c: Symmetric(g0,g0,g-2)
    c: Distance(g1) = 94
    c: Distance(g0) = 44
FEATURE [PartDesign::Pad] Pad
  ClaimChildren = false
  Length = 600
  Length2 = 100
  Profile = -> Sketch
  Type = 0
FEATURE [Sketcher::SketchObject] Sketch001
  ExternalGeometry = -> [Pad]
  MapMode = 5
  Placement = pos=(22,0,0) rot=(0.57735,0.57735,0.57735;2.0944rad)
  Support = -> [Pad]
  expr: Constraints[4] = 45 / 2
  sketch-geometry (2):
    g0: Circle CenterX=-24.5 CenterY=594 CenterZ=0 NormalX=0 NormalY=0 NormalZ=1 AngleXU=0 Radius=1.5
    g1: Circle CenterX=-24.5 CenterY=170 CenterZ=0 NormalX=0 NormalY=0 NormalZ=1 AngleXU=0 Radius=1.5
  constraints (6):
    c: Equal(g1,g0)
    c: DistanceY(g0,g-3) = 6
    c: DistanceY(g1,g-3) = 430
    c: Diameter(g0) = 3
    c: DistanceX(g-3,g0) = 22.5
    c: Vertical(g1,g0)
FEATURE [PartDesign::Pocket] Pocket
  BaseFeature = -> Pad
  ClaimChildren = false
  Length = 10
  Length2 = 100
  Profile = -> Sketch001
  Type = 0
FEATURE [Sketcher::SketchObject] Sketch002
  ExternalGeometry = -> [Pocket]
  MapMode = 5
  Placement = pos=(0,0,0) rot=(1,0,0;3.14159rad)
  Support = -> [Pocket]
  sketch-geometry (2):
    g0: Circle CenterX=0 CenterY=27 CenterZ=0 NormalX=0 NormalY=0 NormalZ=1 AngleXU=0 Radius=1.5
    g1: Circle CenterX=0 CenterY=-27 CenterZ=0 NormalX=0 NormalY=0 NormalZ=1 AngleXU=0 Radius=1.5
  constraints (5):
    c: PointOnObject(g0,g-2)
    c: Equal(g0,g1)
    c: Symmetric(g1,g0,g-1)
    c: DistanceY(g0,g-3) = 20
    c: Diameter(g0) = 3
FEATURE [PartDesign::Pocket] Pocket001
  BaseFeature = -> Pocket
  ClaimChildren = false
  Length = 10
  Length2 = 100
  Profile = -> Sketch002
  Type = 0
FEATURE [Sketcher::SketchObject] Sketch003
  ExternalGeometry = -> [Pocket001]
  MapMode = 5
  Placement = pos=(22,0,0) rot=(0.57735,0.57735,0.57735;2.0944rad)
  Support = -> [Pocket001]
  expr: Constraints[4] = 45 / 2
  sketch-geometry (3):
    g0: Circle CenterX=24.5 CenterY=530 CenterZ=0 NormalX=0 NormalY=0 NormalZ=1 AngleXU=0 Radius=1.5
    g1: Circle CenterX=24.5 CenterY=370 CenterZ=0 NormalX=0 NormalY=0 NormalZ=1 AngleXU=0 Radius=1.5
    g2: Circle CenterX=24.5 CenterY=18 CenterZ=0 NormalX=0 NormalY=0 NormalZ=1 AngleXU=0 Radius=1.5
  constraints (9):
    c: Equal(g0,g1)
    c: Equal(g1,g2)
    c: Vertical(g2,g1)
    c: Vertical(g1,g0)
    c: DistanceX(g0,g-3) = 22.5
    c: DistanceY(g0,g-3) = 70
    c: DistanceY(g1,g0) = 160
    c: DistanceY(g2,g1) = 352
    c: Diameter(g0) = 3
FEATURE [PartDesign::Pocket] Pocket002
  BaseFeature = -> Pocket001
  ClaimChildren = false
  Length = 10
  Length2 = 100
  Profile = -> Sketch003
  Type = 0
FEATURE [Sketcher::SketchObject] Sketch004
  ExternalGeometry = -> [Pocket002]
  MapMode = 5
  Placement = pos=(22,0,0) rot=(0.57735,0.57735,0.57735;2.0944rad)
  Support = -> [Pocket002]
  expr: Constraints[2] = 45 / 2
  sketch-geometry (1):
    g0: Circle CenterX=24.5 CenterY=550 CenterZ=0 NormalX=0 NormalY=0 NormalZ=1 AngleXU=0 Radius=3
  constraints (3):
    c: DistanceY(g0,g-3) = 50
    c: Diameter(g0) = 6
    c: DistanceX(g0,g-3) = 22.5
FEATURE [PartDesign::Pocket] Pocket003
  BaseFeature = -> Pocket002
  ClaimChildren = false
  Length = 5
  Length2 = 100
  Profile = -> Sketch004
  Type = 1
FEATURE [PartDesign::Body] Body  label="right beam"
  Group = -> [Sketch,Pad,Sketch001,Pocket,Sketch002,Pocket001,Sketch003,Pocket002,Sketch004,Pocket003]
  Origin = -> Origin
  SingleSolid = true
  Tip = -> Pocket003
FEATURE [Part::Mirroring] Part__Mirroring  label="left beam"
  Base = (0,0,0)
  Normal = (1,0,0)
  Placement = pos=(-121,0,0) rot=(0,0,1;0rad)
  Source = -> Pocket003
FEATURE [App::FeaturePython] Constraints  # WARN: FeaturePython — macro-defined, semantics opaque (R4)
  GroupMode = 1
  _Version = 1
FEATURE [Part::FeaturePython] Parts  # WARN: FeaturePython — macro-defined, semantics opaque (R4)
  Group = -> [Origin001,Part__Mirroring]
  GroupMode = 0
FEATURE [App::FeaturePython] Constraints001  # WARN: FeaturePython — macro-defined, semantics opaque (R4)
  GroupMode = 1
  _Version = 1
FEATURE [Part::FeaturePython] Parts001  # WARN: FeaturePython — macro-defined, semantics opaque (R4)
  Group = -> [Origin002,Body]
  GroupMode = 0
FEATURE [Part::FeaturePython] Assembly  label="middle-stage-beam-right"  # WARN: FeaturePython — macro-defined, semantics opaque (R4)
  AutoRelax = true
  BuildShape = 0
  Freeze = false
  Group = -> [Constraints,Elements,Parts]
  GroupMode = 1
  SolverType = 1
  Verbose = false
  _SolverType = 1
  _Version = 1
FEATURE [App::FeaturePython] Elements  # WARN: FeaturePython — macro-defined, semantics opaque (R4)
  Group = -> [Element008,Element009,Element010,Element011,Element012,Element013,Element014,Element015]
  GroupMode = 1
FEATURE [Part::FeaturePython] Assembly001  label="middle-stage-beam-left"  # WARN: FeaturePython — macro-defined, semantics opaque (R4)
  AutoRelax = true
  BuildShape = 0
  Freeze = false
  Group = -> [Constraints001,Elements001,Parts001]
  GroupMode = 1
  SolverType = 1
  Verbose = false
  _SolverType = 1
  _Version = 1
FEATURE [App::FeaturePython] Elements001  # WARN: FeaturePython — macro-defined, semantics opaque (R4)
  Group = -> [Element,Element001,Element002,Element003,Element004,Element005,Element006,Element007]
  GroupMode = 1
FEATURE [Part::FeaturePython] Element  label="actuator-rod-hole"  # link proxy (typed FeaturePython)
  Detach = false
  LinkTransform = true
  LinkedObject = -> Body [Pocket003.Sketch004.Edge1]
  _Parent = -> Elements001
FEATURE [Part::FeaturePython] Element001  label="rail_upper_top"  # link proxy (typed FeaturePython)
  Detach = false
  LinkTransform = true
  LinkedObject = -> Body [Pocket.Sketch001.Edge1]
  _Parent = -> Elements001
FEATURE [Part::FeaturePython] Element002  label="rail_upper_bottom"  # link proxy (typed FeaturePython)
  Detach = false
  LinkTransform = true
  LinkedObject = -> Body [Pocket.Sketch001.Edge2]
  _Parent = -> Elements001
FEATURE [Part::FeaturePython] Element003  label="rail_middle_top"  # link proxy (typed FeaturePython)
  Detach = false
  LinkTransform = true
  LinkedObject = -> Body [Pocket002.Sketch003.Edge1]
  _Parent = -> Elements001
FEATURE [Part::FeaturePython] Element004  label="rail_middle_middle"  # link proxy (typed FeaturePython)
  Detach = false
  LinkTransform = true
  LinkedObject = -> Body [Pocket002.Sketch003.Edge2]
  _Parent = -> Elements001
FEATURE [Part::FeaturePython] Element005  label="rail_middle_bottom"  # link proxy (typed FeaturePython)
  Detach = false
  LinkTransform = true
  LinkedObject = -> Body [Pocket002.Sketch003.Edge3]
  _Parent = -> Elements001
FEATURE [Part::FeaturePython] Element006  label="base_mount_front"  # link proxy (typed FeaturePython)
  Detach = false
  LinkTransform = true
  LinkedObject = -> Body [Pocket001.Sketch002.Edge1]
  _Parent = -> Elements001
FEATURE [Part::FeaturePython] Element007  label="base_mount_rear"  # link proxy (typed FeaturePython)
  Detach = false
  LinkTransform = true
  LinkedObject = -> Body [Pocket001.Sketch002.Edge2]
  _Parent = -> Elements001
FEATURE [Part::FeaturePython] Element008  label="actuator_rod_hole"  # link proxy (typed FeaturePython)
  Detach = false
  LinkTransform = true
  LinkedObject = -> Part__Mirroring [Edge13]
  _Parent = -> Elements
FEATURE [Part::FeaturePython] Element009  label="rail_upper_top"  # link proxy (typed FeaturePython)
  Detach = false
  LinkTransform = true
  LinkedObject = -> Part__Mirroring [Edge14]
  _Parent = -> Elements
FEATURE [Part::FeaturePython] Element010  label="rail_upper_bottom"  # link proxy (typed FeaturePython)
  Detach = false
  LinkTransform = true
  LinkedObject = -> Part__Mirroring [Edge15]
  _Parent = -> Elements
FEATURE [Part::FeaturePython] Element011  label="rail_middle_top"  # link proxy (typed FeaturePython)
  Detach = false
  LinkTransform = true
  LinkedObject = -> Part__Mirroring [Edge12]
  _Parent = -> Elements
FEATURE [Part::FeaturePython] Element012  label="rail_middle_middle"  # link proxy (typed FeaturePython)
  Detach = false
  LinkTransform = true
  LinkedObject = -> Part__Mirroring [Edge16]
  _Parent = -> Elements
FEATURE [Part::FeaturePython] Element013  label="rail_middle_bottom"  # link proxy (typed FeaturePython)
  Detach = false
  LinkTransform = true
  LinkedObject = -> Part__Mirroring [Edge17]
  _Parent = -> Elements
FEATURE [Part::FeaturePython] Element014  label="base_mount_front"  # link proxy (typed FeaturePython)
  Detach = false
  LinkTransform = true
  LinkedObject = -> Part__Mirroring [Edge20]
  _Parent = -> Elements
FEATURE [Part::FeaturePython] Element015  label="base_mount_rear"  # link proxy (typed FeaturePython)
  Detach = false
  LinkTransform = true
  LinkedObject = -> Part__Mirroring [Edge19]
  _Parent = -> Elements
